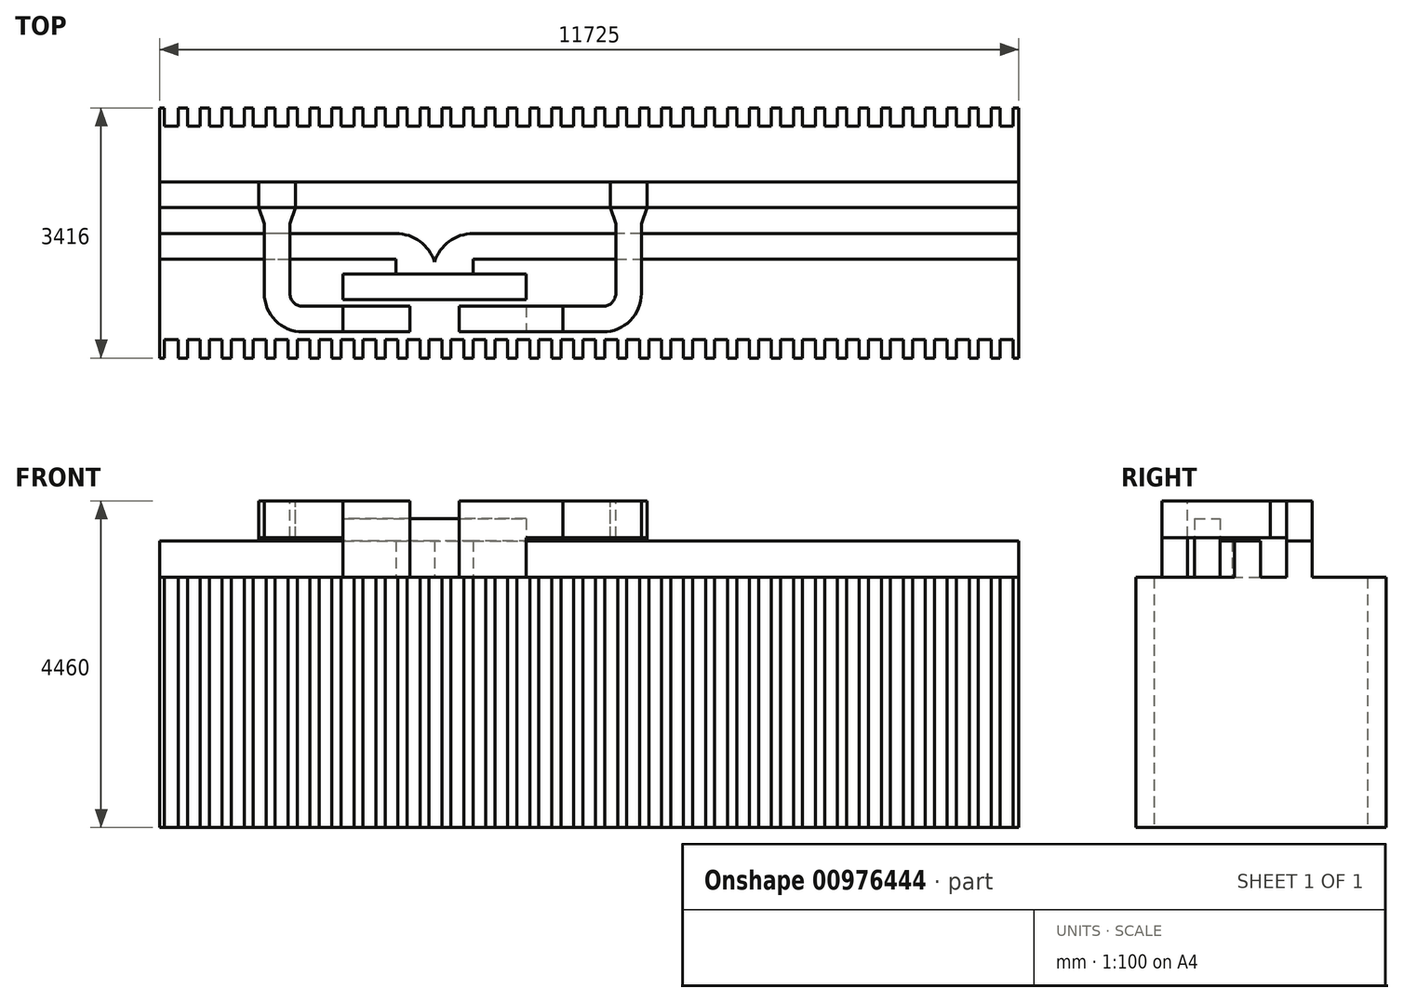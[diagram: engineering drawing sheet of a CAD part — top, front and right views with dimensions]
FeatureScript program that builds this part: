
annotation { "Feature Type Name" : "Feature", "Feature Type Description" : "" }
export const myFeature = defineFeature(function(context is Context, id is Id, definition is map)
    precondition{}
    {
        {
            var Q0;
            Q0=qCreatedBy(makeId("Top.planeOp"),FACE);
            var sketch = newSketch(context, id + "F0", { "sketchPlane" : qUnion([Q0])});
            skLineSegment(sketch, "E0.bottom", {"start": v(-25000, 7300) * mm, "end": v(25000, 7300) * mm});
            skLineSegment(sketch, "E0.top", {"start": v(-25000, -7300) * mm, "end": v(25000, -7300) * mm});
            skLineSegment(sketch, "E0.left", {"start": v(-25000, 7300) * mm, "end": v(-25000, -7300) * mm});
            skLineSegment(sketch, "E0.right", {"start": v(25000, 7300) * mm, "end": v(25000, -7300) * mm});
            skPoint(sketch, "E0.middle", {"position": v(0, 0) * mm});
            skSolve(sketch);
        }
        {
            var Q0;
            Q0=makeQuery(id+"F0.imprint","IMPRINT",FACE,{"disambiguationData":[TD([[makeQuery(id+"F0.imprint","IMPRINT",EDGE,{"derivedFrom":sQuery(id+"F0.wireOp",EDGE,"E0.bottom")}),-1.0]])]});
            var sketch = newSketch(context, id + "F1", { "sketchPlane" : qUnion([Q0])});
            skLineSegment(sketch, "E1", {"start": v(-20201.46, 5909) * mm, "end": v(-20138.96, 5909) * mm});
            skLineSegment(sketch, "E2", {"start": v(-20201.46, 5909) * mm, "end": v(-20201.46, 2493) * mm});
            skLineSegment(sketch, "E3", {"start": v(-20201.46, 2493) * mm, "end": v(-20138.96, 2493) * mm});
            skLineSegment(sketch, "E4", {"start": v(-8476.46, 2493) * mm, "end": v(-8476.46, 5909) * mm});
            skLineSegment(sketch, "E5.0", {"start": v(-20138.96, 5909) * mm, "end": v(-20138.96, 2493) * mm});
            skLineSegment(sketch, "E6.0", {"start": v(-19951.46, 5909) * mm, "end": v(-19951.46, 2493) * mm});
            skLineSegment(sketch, "E7.0", {"start": v(-19651.46, 5909) * mm, "end": v(-19651.46, 2493) * mm});
            skLineSegment(sketch, "E8.0", {"start": v(-19351.46, 5909) * mm, "end": v(-19351.46, 2493) * mm});
            skLineSegment(sketch, "E9.0", {"start": v(-19051.46, 5909) * mm, "end": v(-19051.46, 2493) * mm});
            skLineSegment(sketch, "E10.0", {"start": v(-18751.46, 5909) * mm, "end": v(-18751.46, 2493) * mm});
            skLineSegment(sketch, "E11.0", {"start": v(-18451.46, 5909) * mm, "end": v(-18451.46, 2493) * mm});
            skLineSegment(sketch, "E12.0", {"start": v(-18151.46, 5909) * mm, "end": v(-18151.46, 2493) * mm});
            skLineSegment(sketch, "E13.0", {"start": v(-17851.46, 5909) * mm, "end": v(-17851.46, 2493) * mm});
            skLineSegment(sketch, "E14.0", {"start": v(-17551.46, 5909) * mm, "end": v(-17551.46, 2493) * mm});
            skLineSegment(sketch, "E15.0", {"start": v(-17251.46, 5909) * mm, "end": v(-17251.46, 2493) * mm});
            skLineSegment(sketch, "E16.0", {"start": v(-16951.46, 5909) * mm, "end": v(-16951.46, 2493) * mm});
            skLineSegment(sketch, "E17.0", {"start": v(-16651.46, 5909) * mm, "end": v(-16651.46, 2493) * mm});
            skLineSegment(sketch, "E18.0", {"start": v(-16351.46, 5909) * mm, "end": v(-16351.46, 2493) * mm});
            skLineSegment(sketch, "E19.0", {"start": v(-16051.46, 5909) * mm, "end": v(-16051.46, 2493) * mm});
            skLineSegment(sketch, "E20.0", {"start": v(-15751.46, 5909) * mm, "end": v(-15751.46, 2493) * mm});
            skLineSegment(sketch, "E21.0", {"start": v(-25005, 7305) * mm, "end": v(-25005, -7305) * mm});
            skLineSegment(sketch, "E21.1", {"start": v(25005, 7305) * mm, "end": v(-25005, 7305) * mm});
            skLineSegment(sketch, "E21.2", {"start": v(25005, -7305) * mm, "end": v(25005, 7305) * mm});
            skLineSegment(sketch, "E21.3", {"start": v(-25005, -7305) * mm, "end": v(25005, -7305) * mm});
            skLineSegment(sketch, "E22.0", {"start": v(-15451.46, 5909) * mm, "end": v(-15451.46, 2493) * mm});
            skLineSegment(sketch, "E23.0", {"start": v(-15151.46, 5909) * mm, "end": v(-15151.46, 2493) * mm});
            skLineSegment(sketch, "E24.0", {"start": v(-14851.46, 5909) * mm, "end": v(-14851.46, 2493) * mm});
            skLineSegment(sketch, "E25.0", {"start": v(-14551.46, 5909) * mm, "end": v(-14551.46, 2493) * mm});
            skLineSegment(sketch, "E26.0", {"start": v(-14251.46, 5909) * mm, "end": v(-14251.46, 2493) * mm});
            skLineSegment(sketch, "E27.0", {"start": v(-13951.46, 5909) * mm, "end": v(-13951.46, 2493) * mm});
            skLineSegment(sketch, "E28.0", {"start": v(-13651.46, 5909) * mm, "end": v(-13651.46, 2493) * mm});
            skLineSegment(sketch, "E29.0", {"start": v(-13351.46, 5909) * mm, "end": v(-13351.46, 2493) * mm});
            skLineSegment(sketch, "E30.0", {"start": v(-13051.46, 5909) * mm, "end": v(-13051.46, 2493) * mm});
            skLineSegment(sketch, "E31.0", {"start": v(-12751.46, 5909) * mm, "end": v(-12751.46, 2493) * mm});
            skLineSegment(sketch, "E32.0", {"start": v(-12451.46, 5909) * mm, "end": v(-12451.46, 2493) * mm});
            skLineSegment(sketch, "E33.0", {"start": v(-12151.46, 5909) * mm, "end": v(-12151.46, 2493) * mm});
            skLineSegment(sketch, "E34.0", {"start": v(-11851.46, 5909) * mm, "end": v(-11851.46, 2493) * mm});
            skLineSegment(sketch, "E35.0", {"start": v(-11551.46, 5909) * mm, "end": v(-11551.46, 2493) * mm});
            skLineSegment(sketch, "E36.0", {"start": v(-11251.46, 5909) * mm, "end": v(-11251.46, 2493) * mm});
            skLineSegment(sketch, "E37.0", {"start": v(-10951.46, 5909) * mm, "end": v(-10951.46, 2493) * mm});
            skLineSegment(sketch, "E38.0", {"start": v(-10651.46, 5909) * mm, "end": v(-10651.46, 2493) * mm});
            skLineSegment(sketch, "E39.0", {"start": v(-10351.46, 5909) * mm, "end": v(-10351.46, 2493) * mm});
            skLineSegment(sketch, "E40.0", {"start": v(-10051.46, 5909) * mm, "end": v(-10051.46, 2493) * mm});
            skLineSegment(sketch, "E41.0", {"start": v(-9751.46, 5909) * mm, "end": v(-9751.46, 2493) * mm});
            skLineSegment(sketch, "E42.0", {"start": v(-9451.46, 5909) * mm, "end": v(-9451.46, 2493) * mm});
            skLineSegment(sketch, "E43.0", {"start": v(-9151.46, 5909) * mm, "end": v(-9151.46, 2493) * mm});
            skLineSegment(sketch, "E44.0", {"start": v(-8851.46, 5909) * mm, "end": v(-8851.46, 2493) * mm});
            skLineSegment(sketch, "E45.0", {"start": v(-8551.46, 5909) * mm, "end": v(-8551.46, 2493) * mm});
            skLineSegment(sketch, "E46.0", {"start": v(-19826.46, 5909) * mm, "end": v(-19826.46, 2493) * mm});
            skLineSegment(sketch, "E47.0", {"start": v(-19526.46, 5909) * mm, "end": v(-19526.46, 2493) * mm});
            skLineSegment(sketch, "E48.0", {"start": v(-19226.46, 5909) * mm, "end": v(-19226.46, 2493) * mm});
            skLineSegment(sketch, "E49.0", {"start": v(-18926.46, 5909) * mm, "end": v(-18926.46, 2493) * mm});
            skLineSegment(sketch, "E50.0", {"start": v(-18626.46, 5909) * mm, "end": v(-18626.46, 2493) * mm});
            skLineSegment(sketch, "E51.0", {"start": v(-18326.46, 5909) * mm, "end": v(-18326.46, 2493) * mm});
            skLineSegment(sketch, "E52.0", {"start": v(-18026.46, 5909) * mm, "end": v(-18026.46, 2493) * mm});
            skLineSegment(sketch, "E53.0", {"start": v(-17726.46, 5909) * mm, "end": v(-17726.46, 2493) * mm});
            skLineSegment(sketch, "E54.0", {"start": v(-17426.46, 5909) * mm, "end": v(-17426.46, 2493) * mm});
            skLineSegment(sketch, "E55.0", {"start": v(-17126.46, 5909) * mm, "end": v(-17126.46, 2493) * mm});
            skLineSegment(sketch, "E56.0", {"start": v(-16826.46, 5909) * mm, "end": v(-16826.46, 2493) * mm});
            skLineSegment(sketch, "E57.0", {"start": v(-16526.46, 5909) * mm, "end": v(-16526.46, 2493) * mm});
            skLineSegment(sketch, "E58.0", {"start": v(-16226.46, 5909) * mm, "end": v(-16226.46, 2493) * mm});
            skLineSegment(sketch, "E59.0", {"start": v(-15926.46, 5909) * mm, "end": v(-15926.46, 2493) * mm});
            skLineSegment(sketch, "E60.0", {"start": v(-15626.46, 5909) * mm, "end": v(-15626.46, 2493) * mm});
            skLineSegment(sketch, "E61.0", {"start": v(-15326.46, 5909) * mm, "end": v(-15326.46, 2493) * mm});
            skLineSegment(sketch, "E62.0", {"start": v(-15026.46, 5909) * mm, "end": v(-15026.46, 2493) * mm});
            skLineSegment(sketch, "E63.0", {"start": v(-14726.46, 5909) * mm, "end": v(-14726.46, 2493) * mm});
            skLineSegment(sketch, "E64.0", {"start": v(-14426.46, 5909) * mm, "end": v(-14426.46, 2493) * mm});
            skLineSegment(sketch, "E65.0", {"start": v(-14126.46, 5909) * mm, "end": v(-14126.46, 2493) * mm});
            skLineSegment(sketch, "E66.0", {"start": v(-13826.46, 5909) * mm, "end": v(-13826.46, 2493) * mm});
            skLineSegment(sketch, "E67.0", {"start": v(-13526.46, 5909) * mm, "end": v(-13526.46, 2493) * mm});
            skLineSegment(sketch, "E68.0", {"start": v(-13226.46, 5909) * mm, "end": v(-13226.46, 2493) * mm});
            skLineSegment(sketch, "E69.0", {"start": v(-12926.46, 5909) * mm, "end": v(-12926.46, 2493) * mm});
            skLineSegment(sketch, "E70.0", {"start": v(-12626.46, 5909) * mm, "end": v(-12626.46, 2493) * mm});
            skLineSegment(sketch, "E71.0", {"start": v(-12326.46, 5909) * mm, "end": v(-12326.46, 2493) * mm});
            skLineSegment(sketch, "E72.0", {"start": v(-12026.46, 5909) * mm, "end": v(-12026.46, 2493) * mm});
            skLineSegment(sketch, "E73.0", {"start": v(-11726.46, 5909) * mm, "end": v(-11726.46, 2493) * mm});
            skLineSegment(sketch, "E74.0", {"start": v(-11426.46, 5909) * mm, "end": v(-11426.46, 2493) * mm});
            skLineSegment(sketch, "E75.0", {"start": v(-11126.46, 5909) * mm, "end": v(-11126.46, 2493) * mm});
            skLineSegment(sketch, "E76.0", {"start": v(-10826.46, 5909) * mm, "end": v(-10826.46, 2493) * mm});
            skLineSegment(sketch, "E77.0", {"start": v(-10526.46, 5909) * mm, "end": v(-10526.46, 2493) * mm});
            skLineSegment(sketch, "E78.0", {"start": v(-10226.46, 5909) * mm, "end": v(-10226.46, 2493) * mm});
            skLineSegment(sketch, "E79.0", {"start": v(-9926.46, 5909) * mm, "end": v(-9926.46, 2493) * mm});
            skLineSegment(sketch, "E80.0", {"start": v(-9626.46, 5909) * mm, "end": v(-9626.46, 2493) * mm});
            skLineSegment(sketch, "E81.0", {"start": v(-9326.46, 5909) * mm, "end": v(-9326.46, 2493) * mm});
            skLineSegment(sketch, "E82.0", {"start": v(-9026.46, 5909) * mm, "end": v(-9026.46, 2493) * mm});
            skLineSegment(sketch, "E83.0", {"start": v(-8726.46, 5909) * mm, "end": v(-8726.46, 2493) * mm});
            skLineSegment(sketch, "E84", {"start": v(-20201.46, 5659) * mm, "end": v(-8476.46, 5659) * mm});
            skLineSegment(sketch, "E85", {"start": v(-20201.46, 2743) * mm, "end": v(-8476.46, 2743) * mm});
            skLineSegment(sketch, "E86.trimOffspring", {"start": v(-8551.46, 5909) * mm, "end": v(-8476.46, 5909) * mm});
            skLineSegment(sketch, "E87.trimOffspring", {"start": v(-8851.46, 5909) * mm, "end": v(-8726.46, 5909) * mm});
            skLineSegment(sketch, "E88.trimOffspring", {"start": v(-9151.46, 5909) * mm, "end": v(-9026.46, 5909) * mm});
            skLineSegment(sketch, "E89.trimOffspring", {"start": v(-9451.46, 5909) * mm, "end": v(-9326.46, 5909) * mm});
            skLineSegment(sketch, "E90.trimOffspring", {"start": v(-9751.46, 5909) * mm, "end": v(-9626.46, 5909) * mm});
            skLineSegment(sketch, "E91.trimOffspring", {"start": v(-10051.46, 5909) * mm, "end": v(-9926.46, 5909) * mm});
            skLineSegment(sketch, "E92.trimOffspring", {"start": v(-10351.46, 5909) * mm, "end": v(-10226.46, 5909) * mm});
            skLineSegment(sketch, "E93.trimOffspring", {"start": v(-10651.46, 5909) * mm, "end": v(-10526.46, 5909) * mm});
            skLineSegment(sketch, "E94.trimOffspring", {"start": v(-10951.46, 5909) * mm, "end": v(-10826.46, 5909) * mm});
            skLineSegment(sketch, "E95.trimOffspring", {"start": v(-11251.46, 5909) * mm, "end": v(-11126.46, 5909) * mm});
            skLineSegment(sketch, "E96.trimOffspring", {"start": v(-11551.46, 5909) * mm, "end": v(-11426.46, 5909) * mm});
            skLineSegment(sketch, "E97.trimOffspring", {"start": v(-11851.46, 5909) * mm, "end": v(-11726.46, 5909) * mm});
            skLineSegment(sketch, "E98.trimOffspring", {"start": v(-12151.46, 5909) * mm, "end": v(-12026.46, 5909) * mm});
            skLineSegment(sketch, "E99.trimOffspring", {"start": v(-12451.46, 5909) * mm, "end": v(-12326.46, 5909) * mm});
            skLineSegment(sketch, "E100.trimOffspring", {"start": v(-12751.46, 5909) * mm, "end": v(-12626.46, 5909) * mm});
            skLineSegment(sketch, "E101.trimOffspring", {"start": v(-13051.46, 5909) * mm, "end": v(-12926.46, 5909) * mm});
            skLineSegment(sketch, "E102.trimOffspring", {"start": v(-13351.46, 5909) * mm, "end": v(-13226.46, 5909) * mm});
            skLineSegment(sketch, "E103.trimOffspring", {"start": v(-13651.46, 5909) * mm, "end": v(-13526.46, 5909) * mm});
            skLineSegment(sketch, "E104.trimOffspring", {"start": v(-13951.46, 5909) * mm, "end": v(-13826.46, 5909) * mm});
            skLineSegment(sketch, "E105.trimOffspring", {"start": v(-14251.46, 5909) * mm, "end": v(-14126.46, 5909) * mm});
            skLineSegment(sketch, "E106.trimOffspring", {"start": v(-14551.46, 5909) * mm, "end": v(-14426.46, 5909) * mm});
            skLineSegment(sketch, "E107.trimOffspring", {"start": v(-14851.46, 5909) * mm, "end": v(-14726.46, 5909) * mm});
            skLineSegment(sketch, "E108.trimOffspring", {"start": v(-15151.46, 5909) * mm, "end": v(-15026.46, 5909) * mm});
            skLineSegment(sketch, "E109.trimOffspring", {"start": v(-15451.46, 5909) * mm, "end": v(-15326.46, 5909) * mm});
            skLineSegment(sketch, "E110.trimOffspring", {"start": v(-15751.46, 5909) * mm, "end": v(-15626.46, 5909) * mm});
            skLineSegment(sketch, "E111.trimOffspring", {"start": v(-16051.46, 5909) * mm, "end": v(-15926.46, 5909) * mm});
            skLineSegment(sketch, "E112.trimOffspring", {"start": v(-16351.46, 5909) * mm, "end": v(-16226.46, 5909) * mm});
            skLineSegment(sketch, "E113.trimOffspring", {"start": v(-16651.46, 5909) * mm, "end": v(-16526.46, 5909) * mm});
            skLineSegment(sketch, "E114.trimOffspring", {"start": v(-16951.46, 5909) * mm, "end": v(-16826.46, 5909) * mm});
            skLineSegment(sketch, "E115.trimOffspring", {"start": v(-17251.46, 5909) * mm, "end": v(-17126.46, 5909) * mm});
            skLineSegment(sketch, "E116.trimOffspring", {"start": v(-17551.46, 5909) * mm, "end": v(-17426.46, 5909) * mm});
            skLineSegment(sketch, "E117.trimOffspring", {"start": v(-17851.46, 5909) * mm, "end": v(-17726.46, 5909) * mm});
            skLineSegment(sketch, "E118.trimOffspring", {"start": v(-18151.46, 5909) * mm, "end": v(-18026.46, 5909) * mm});
            skLineSegment(sketch, "E119.trimOffspring", {"start": v(-18451.46, 5909) * mm, "end": v(-18326.46, 5909) * mm});
            skLineSegment(sketch, "E120.trimOffspring", {"start": v(-18751.46, 5909) * mm, "end": v(-18626.46, 5909) * mm});
            skLineSegment(sketch, "E121.trimOffspring", {"start": v(-19051.46, 5909) * mm, "end": v(-18926.46, 5909) * mm});
            skLineSegment(sketch, "E122.trimOffspring", {"start": v(-19351.46, 5909) * mm, "end": v(-19226.46, 5909) * mm});
            skLineSegment(sketch, "E123.trimOffspring", {"start": v(-19651.46, 5909) * mm, "end": v(-19526.46, 5909) * mm});
            skLineSegment(sketch, "E124.trimOffspring", {"start": v(-19951.46, 5909) * mm, "end": v(-19826.46, 5909) * mm});
            skLineSegment(sketch, "E125.trimOffspring", {"start": v(-19651.46, 2493) * mm, "end": v(-19526.46, 2493) * mm});
            skLineSegment(sketch, "E126.trimOffspring", {"start": v(-18751.46, 2493) * mm, "end": v(-18626.46, 2493) * mm});
            skLineSegment(sketch, "E127.trimOffspring", {"start": v(-17851.46, 2493) * mm, "end": v(-17726.46, 2493) * mm});
            skLineSegment(sketch, "E128.trimOffspring", {"start": v(-17251.46, 2493) * mm, "end": v(-17126.46, 2493) * mm});
            skLineSegment(sketch, "E129.trimOffspring", {"start": v(-16351.46, 2493) * mm, "end": v(-16226.46, 2493) * mm});
            skLineSegment(sketch, "E130.trimOffspring", {"start": v(-16951.46, 2493) * mm, "end": v(-16826.46, 2493) * mm});
            skLineSegment(sketch, "E131", {"start": v(-17551.46, 2493) * mm, "end": v(-17426.46, 2493) * mm});
            skLineSegment(sketch, "E132", {"start": v(-16651.46, 2493) * mm, "end": v(-16526.46, 2493) * mm});
            skLineSegment(sketch, "E133.trimOffspring", {"start": v(-15751.46, 2493) * mm, "end": v(-15626.46, 2493) * mm});
            skLineSegment(sketch, "E134.trimOffspring", {"start": v(-14551.46, 2493) * mm, "end": v(-14426.46, 2493) * mm});
            skLineSegment(sketch, "E135.trimOffspring", {"start": v(-15151.46, 2493) * mm, "end": v(-15026.46, 2493) * mm});
            skLineSegment(sketch, "E136.trimOffspring", {"start": v(-15451.46, 2493) * mm, "end": v(-15326.46, 2493) * mm});
            skLineSegment(sketch, "E137", {"start": v(-14851.46, 2493) * mm, "end": v(-14726.46, 2493) * mm});
            skLineSegment(sketch, "E138.trimOffspring", {"start": v(-13951.46, 2493) * mm, "end": v(-13826.46, 2493) * mm});
            skLineSegment(sketch, "E139.trimOffspring", {"start": v(-13351.46, 2493) * mm, "end": v(-13226.46, 2493) * mm});
            skLineSegment(sketch, "E140.trimOffspring", {"start": v(-13651.46, 2493) * mm, "end": v(-13526.46, 2493) * mm});
            skLineSegment(sketch, "E141", {"start": v(-14251.46, 2493) * mm, "end": v(-14126.46, 2493) * mm});
            skLineSegment(sketch, "E142.trimOffspring", {"start": v(-13051.46, 2493) * mm, "end": v(-12926.46, 2493) * mm});
            skLineSegment(sketch, "E143.trimOffspring", {"start": v(-12751.46, 2493) * mm, "end": v(-12626.46, 2493) * mm});
            skLineSegment(sketch, "E144.trimOffspring", {"start": v(-12151.46, 2493) * mm, "end": v(-12026.46, 2493) * mm});
            skLineSegment(sketch, "E145.trimOffspring", {"start": v(-11551.46, 2493) * mm, "end": v(-11426.46, 2493) * mm});
            skLineSegment(sketch, "E146.trimOffspring", {"start": v(-11851.46, 2493) * mm, "end": v(-11726.46, 2493) * mm});
            skLineSegment(sketch, "E147.trimOffspring", {"start": v(-11251.46, 2493) * mm, "end": v(-11126.46, 2493) * mm});
            skLineSegment(sketch, "E148.trimOffspring", {"start": v(-10951.46, 2493) * mm, "end": v(-10826.46, 2493) * mm});
            skLineSegment(sketch, "E149.trimOffspring", {"start": v(-10651.46, 2493) * mm, "end": v(-10526.46, 2493) * mm});
            skLineSegment(sketch, "E150.trimOffspring", {"start": v(-9751.46, 2493) * mm, "end": v(-9626.46, 2493) * mm});
            skLineSegment(sketch, "E151.trimOffspring", {"start": v(-8851.46, 2493) * mm, "end": v(-8726.46, 2493) * mm});
            skLineSegment(sketch, "E152", {"start": v(-10351.46, 2493) * mm, "end": v(-10226.46, 2493) * mm});
            skLineSegment(sketch, "E153", {"start": v(-10051.46, 2493) * mm, "end": v(-9926.46, 2493) * mm});
            skLineSegment(sketch, "E154", {"start": v(-9151.46, 2493) * mm, "end": v(-9026.46, 2493) * mm});
            skLineSegment(sketch, "E155.trimOffspring", {"start": v(-9451.46, 2493) * mm, "end": v(-9326.46, 2493) * mm});
            skLineSegment(sketch, "E156.trimOffspring", {"start": v(-8551.46, 2493) * mm, "end": v(-8476.46, 2493) * mm});
            skLineSegment(sketch, "E157.trimOffspring", {"start": v(-18451.46, 2493) * mm, "end": v(-18326.46, 2493) * mm});
            skLineSegment(sketch, "E158.trimOffspring", {"start": v(-19351.46, 2493) * mm, "end": v(-19226.46, 2493) * mm});
            skLineSegment(sketch, "E159", {"start": v(-19051.46, 2493) * mm, "end": v(-18926.46, 2493) * mm});
            skLineSegment(sketch, "E160", {"start": v(-18151.46, 2493) * mm, "end": v(-18026.46, 2493) * mm});
            skLineSegment(sketch, "E161", {"start": v(-16051.46, 2493) * mm, "end": v(-15926.46, 2493) * mm});
            skLineSegment(sketch, "E162", {"start": v(-19951.46, 2493) * mm, "end": v(-19826.46, 2493) * mm});
            skLineSegment(sketch, "E163", {"start": v(-12451.46, 2493) * mm, "end": v(-12326.46, 2493) * mm});
            skSolve(sketch);
        }
        {
            var Q0;
            {var subQ0=sQuery(id+"F1.wireOp",EDGE,"E88.trimOffspring");Q0=makeQuery(id+"F1.imprint","IMPRINT",FACE,{"disambiguationData":[TD([[makeQuery(id+"F1.imprint","IMPRINT",EDGE,{"derivedFrom":subQ0}),-1.0]])]});}
            var Q1;
            {var subQ0=sQuery(id+"F1.wireOp",EDGE,"E112.trimOffspring");Q1=makeQuery(id+"F1.imprint","IMPRINT",FACE,{"disambiguationData":[TD([[makeQuery(id+"F1.imprint","IMPRINT",EDGE,{"derivedFrom":subQ0}),-1.0]])]});}
            var Q2;
            {var subQ0=sQuery(id+"F1.wireOp",EDGE,"E84");var subQ1=sQuery(id+"F1.wireOp",EDGE,"E38.0");var subQ2=makeQuery(id+"F1.imprint","INTERSECT",VERTEX,{"derivedFrom":[subQ1,subQ0]});Q2=makeQuery(id+"F1.imprint","IMPRINT",FACE,{"disambiguationData":[TD([[makeQuery(id+"F1.imprint","IMPRINT",EDGE,{"disambiguationData":[TD([[subQ2,-1.0]])],"derivedFrom":subQ1}),1.0]])]});}
            var Q3;
            {var subQ0=sQuery(id+"F1.wireOp",EDGE,"E158.trimOffspring");Q3=makeQuery(id+"F1.imprint","IMPRINT",FACE,{"disambiguationData":[TD([[makeQuery(id+"F1.imprint","IMPRINT",EDGE,{"derivedFrom":subQ0}),1.0]])]});}
            var Q4;
            {var subQ0=sQuery(id+"F1.wireOp",EDGE,"E84");var subQ1=sQuery(id+"F1.wireOp",EDGE,"E18.0");var subQ2=makeQuery(id+"F1.imprint","INTERSECT",VERTEX,{"derivedFrom":[subQ1,subQ0]});Q4=makeQuery(id+"F1.imprint","IMPRINT",FACE,{"disambiguationData":[TD([[makeQuery(id+"F1.imprint","IMPRINT",EDGE,{"disambiguationData":[TD([[subQ2,-1.0]])],"derivedFrom":subQ1}),-1.0]])]});}
            var Q5;
            {var subQ0=sQuery(id+"F1.wireOp",EDGE,"E140.trimOffspring");Q5=makeQuery(id+"F1.imprint","IMPRINT",FACE,{"disambiguationData":[TD([[makeQuery(id+"F1.imprint","IMPRINT",EDGE,{"derivedFrom":subQ0}),1.0]])]});}
            var Q6;
            {var subQ0=sQuery(id+"F1.wireOp",EDGE,"E84");var subQ1=sQuery(id+"F1.wireOp",EDGE,"E35.0");var subQ2=makeQuery(id+"F1.imprint","INTERSECT",VERTEX,{"derivedFrom":[subQ1,subQ0]});Q6=makeQuery(id+"F1.imprint","IMPRINT",FACE,{"disambiguationData":[TD([[makeQuery(id+"F1.imprint","IMPRINT",EDGE,{"disambiguationData":[TD([[subQ2,-1.0]])],"derivedFrom":subQ1}),-1.0]])]});}
            var Q7;
            {var subQ0=sQuery(id+"F1.wireOp",EDGE,"E107.trimOffspring");Q7=makeQuery(id+"F1.imprint","IMPRINT",FACE,{"disambiguationData":[TD([[makeQuery(id+"F1.imprint","IMPRINT",EDGE,{"derivedFrom":subQ0}),-1.0]])]});}
            var Q8;
            {var subQ0=sQuery(id+"F1.wireOp",EDGE,"E129.trimOffspring");Q8=makeQuery(id+"F1.imprint","IMPRINT",FACE,{"disambiguationData":[TD([[makeQuery(id+"F1.imprint","IMPRINT",EDGE,{"derivedFrom":subQ0}),1.0]])]});}
            var Q9;
            {var subQ0=sQuery(id+"F1.wireOp",EDGE,"E120.trimOffspring");Q9=makeQuery(id+"F1.imprint","IMPRINT",FACE,{"disambiguationData":[TD([[makeQuery(id+"F1.imprint","IMPRINT",EDGE,{"derivedFrom":subQ0}),-1.0]])]});}
            var Q10;
            {var subQ0=sQuery(id+"F1.wireOp",EDGE,"E115.trimOffspring");Q10=makeQuery(id+"F1.imprint","IMPRINT",FACE,{"disambiguationData":[TD([[makeQuery(id+"F1.imprint","IMPRINT",EDGE,{"derivedFrom":subQ0}),-1.0]])]});}
            var Q11;
            {var subQ0=sQuery(id+"F1.wireOp",EDGE,"E138.trimOffspring");Q11=makeQuery(id+"F1.imprint","IMPRINT",FACE,{"disambiguationData":[TD([[makeQuery(id+"F1.imprint","IMPRINT",EDGE,{"derivedFrom":subQ0}),1.0]])]});}
            var Q12;
            {var subQ0=sQuery(id+"F1.wireOp",EDGE,"E84");var subQ1=sQuery(id+"F1.wireOp",EDGE,"E11.0");var subQ2=makeQuery(id+"F1.imprint","INTERSECT",VERTEX,{"derivedFrom":[subQ1,subQ0]});Q12=makeQuery(id+"F1.imprint","IMPRINT",FACE,{"disambiguationData":[TD([[makeQuery(id+"F1.imprint","IMPRINT",EDGE,{"disambiguationData":[TD([[subQ2,-1.0]])],"derivedFrom":subQ1}),1.0]])]});}
            var Q13;
            {var subQ0=sQuery(id+"F1.wireOp",EDGE,"E91.trimOffspring");Q13=makeQuery(id+"F1.imprint","IMPRINT",FACE,{"disambiguationData":[TD([[makeQuery(id+"F1.imprint","IMPRINT",EDGE,{"derivedFrom":subQ0}),-1.0]])]});}
            var Q14;
            {var subQ0=sQuery(id+"F1.wireOp",EDGE,"E84");var subQ1=sQuery(id+"F1.wireOp",EDGE,"E13.0");var subQ2=makeQuery(id+"F1.imprint","INTERSECT",VERTEX,{"derivedFrom":[subQ1,subQ0]});Q14=makeQuery(id+"F1.imprint","IMPRINT",FACE,{"disambiguationData":[TD([[makeQuery(id+"F1.imprint","IMPRINT",EDGE,{"disambiguationData":[TD([[subQ2,-1.0]])],"derivedFrom":subQ1}),-1.0]])]});}
            var Q15;
            {var subQ0=sQuery(id+"F1.wireOp",EDGE,"E84");var subQ1=sQuery(id+"F1.wireOp",EDGE,"E26.0");var subQ2=makeQuery(id+"F1.imprint","INTERSECT",VERTEX,{"derivedFrom":[subQ1,subQ0]});Q15=makeQuery(id+"F1.imprint","IMPRINT",FACE,{"disambiguationData":[TD([[makeQuery(id+"F1.imprint","IMPRINT",EDGE,{"disambiguationData":[TD([[subQ2,-1.0]])],"derivedFrom":subQ1}),-1.0]])]});}
            var Q16;
            {var subQ0=sQuery(id+"F1.wireOp",EDGE,"E121.trimOffspring");Q16=makeQuery(id+"F1.imprint","IMPRINT",FACE,{"disambiguationData":[TD([[makeQuery(id+"F1.imprint","IMPRINT",EDGE,{"derivedFrom":subQ0}),-1.0]])]});}
            var Q17;
            {var subQ0=sQuery(id+"F1.wireOp",EDGE,"E130.trimOffspring");Q17=makeQuery(id+"F1.imprint","IMPRINT",FACE,{"disambiguationData":[TD([[makeQuery(id+"F1.imprint","IMPRINT",EDGE,{"derivedFrom":subQ0}),1.0]])]});}
            var Q18;
            {var subQ0=sQuery(id+"F1.wireOp",EDGE,"E154");Q18=makeQuery(id+"F1.imprint","IMPRINT",FACE,{"disambiguationData":[TD([[makeQuery(id+"F1.imprint","IMPRINT",EDGE,{"derivedFrom":subQ0}),1.0]])]});}
            var Q19;
            {var subQ0=sQuery(id+"F1.wireOp",EDGE,"E151.trimOffspring");Q19=makeQuery(id+"F1.imprint","IMPRINT",FACE,{"disambiguationData":[TD([[makeQuery(id+"F1.imprint","IMPRINT",EDGE,{"derivedFrom":subQ0}),1.0]])]});}
            var Q20;
            {var subQ0=sQuery(id+"F1.wireOp",EDGE,"E84");var subQ1=sQuery(id+"F1.wireOp",EDGE,"E30.0");var subQ2=makeQuery(id+"F1.imprint","INTERSECT",VERTEX,{"derivedFrom":[subQ1,subQ0]});Q20=makeQuery(id+"F1.imprint","IMPRINT",FACE,{"disambiguationData":[TD([[makeQuery(id+"F1.imprint","IMPRINT",EDGE,{"disambiguationData":[TD([[subQ2,-1.0]])],"derivedFrom":subQ1}),-1.0]])]});}
            var Q21;
            {var subQ0=sQuery(id+"F1.wireOp",EDGE,"E84");var subQ1=sQuery(id+"F1.wireOp",EDGE,"E19.0");var subQ2=makeQuery(id+"F1.imprint","INTERSECT",VERTEX,{"derivedFrom":[subQ1,subQ0]});Q21=makeQuery(id+"F1.imprint","IMPRINT",FACE,{"disambiguationData":[TD([[makeQuery(id+"F1.imprint","IMPRINT",EDGE,{"disambiguationData":[TD([[subQ2,-1.0]])],"derivedFrom":subQ1}),1.0]])]});}
            var Q22;
            {var subQ0=sQuery(id+"F1.wireOp",EDGE,"E84");var subQ1=sQuery(id+"F1.wireOp",EDGE,"E14.0");var subQ2=makeQuery(id+"F1.imprint","INTERSECT",VERTEX,{"derivedFrom":[subQ1,subQ0]});Q22=makeQuery(id+"F1.imprint","IMPRINT",FACE,{"disambiguationData":[TD([[makeQuery(id+"F1.imprint","IMPRINT",EDGE,{"disambiguationData":[TD([[subQ2,-1.0]])],"derivedFrom":subQ1}),-1.0]])]});}
            var Q23;
            {var subQ0=sQuery(id+"F1.wireOp",EDGE,"E84");var subQ1=sQuery(id+"F1.wireOp",EDGE,"E12.0");var subQ2=makeQuery(id+"F1.imprint","INTERSECT",VERTEX,{"derivedFrom":[subQ1,subQ0]});Q23=makeQuery(id+"F1.imprint","IMPRINT",FACE,{"disambiguationData":[TD([[makeQuery(id+"F1.imprint","IMPRINT",EDGE,{"disambiguationData":[TD([[subQ2,-1.0]])],"derivedFrom":subQ1}),1.0]])]});}
            var Q24;
            {var subQ0=sQuery(id+"F1.wireOp",EDGE,"E143.trimOffspring");Q24=makeQuery(id+"F1.imprint","IMPRINT",FACE,{"disambiguationData":[TD([[makeQuery(id+"F1.imprint","IMPRINT",EDGE,{"derivedFrom":subQ0}),1.0]])]});}
            var Q25;
            {var subQ0=sQuery(id+"F1.wireOp",EDGE,"E161");Q25=makeQuery(id+"F1.imprint","IMPRINT",FACE,{"disambiguationData":[TD([[makeQuery(id+"F1.imprint","IMPRINT",EDGE,{"derivedFrom":subQ0}),1.0]])]});}
            var Q26;
            {var subQ0=sQuery(id+"F1.wireOp",EDGE,"E100.trimOffspring");Q26=makeQuery(id+"F1.imprint","IMPRINT",FACE,{"disambiguationData":[TD([[makeQuery(id+"F1.imprint","IMPRINT",EDGE,{"derivedFrom":subQ0}),-1.0]])]});}
            var Q27;
            {var subQ0=sQuery(id+"F1.wireOp",EDGE,"E84");var subQ1=sQuery(id+"F1.wireOp",EDGE,"E15.0");var subQ2=makeQuery(id+"F1.imprint","INTERSECT",VERTEX,{"derivedFrom":[subQ1,subQ0]});Q27=makeQuery(id+"F1.imprint","IMPRINT",FACE,{"disambiguationData":[TD([[makeQuery(id+"F1.imprint","IMPRINT",EDGE,{"disambiguationData":[TD([[subQ2,-1.0]])],"derivedFrom":subQ1}),-1.0]])]});}
            var Q28;
            {var subQ0=sQuery(id+"F1.wireOp",EDGE,"E84");var subQ1=sQuery(id+"F1.wireOp",EDGE,"E39.0");var subQ2=makeQuery(id+"F1.imprint","INTERSECT",VERTEX,{"derivedFrom":[subQ1,subQ0]});Q28=makeQuery(id+"F1.imprint","IMPRINT",FACE,{"disambiguationData":[TD([[makeQuery(id+"F1.imprint","IMPRINT",EDGE,{"disambiguationData":[TD([[subQ2,-1.0]])],"derivedFrom":subQ1}),1.0]])]});}
            var Q29;
            {var subQ0=sQuery(id+"F1.wireOp",EDGE,"E84");var subQ1=sQuery(id+"F1.wireOp",EDGE,"E36.0");var subQ2=makeQuery(id+"F1.imprint","INTERSECT",VERTEX,{"derivedFrom":[subQ1,subQ0]});Q29=makeQuery(id+"F1.imprint","IMPRINT",FACE,{"disambiguationData":[TD([[makeQuery(id+"F1.imprint","IMPRINT",EDGE,{"disambiguationData":[TD([[subQ2,-1.0]])],"derivedFrom":subQ1}),1.0]])]});}
            var Q30;
            {var subQ0=sQuery(id+"F1.wireOp",EDGE,"E84");var subQ1=sQuery(id+"F1.wireOp",EDGE,"E40.0");var subQ2=makeQuery(id+"F1.imprint","INTERSECT",VERTEX,{"derivedFrom":[subQ1,subQ0]});Q30=makeQuery(id+"F1.imprint","IMPRINT",FACE,{"disambiguationData":[TD([[makeQuery(id+"F1.imprint","IMPRINT",EDGE,{"disambiguationData":[TD([[subQ2,-1.0]])],"derivedFrom":subQ1}),1.0]])]});}
            var Q31;
            {var subQ0=sQuery(id+"F1.wireOp",EDGE,"E118.trimOffspring");Q31=makeQuery(id+"F1.imprint","IMPRINT",FACE,{"disambiguationData":[TD([[makeQuery(id+"F1.imprint","IMPRINT",EDGE,{"derivedFrom":subQ0}),-1.0]])]});}
            var Q32;
            {var subQ0=sQuery(id+"F1.wireOp",EDGE,"E84");var subQ1=sQuery(id+"F1.wireOp",EDGE,"E10.0");var subQ2=makeQuery(id+"F1.imprint","INTERSECT",VERTEX,{"derivedFrom":[subQ1,subQ0]});Q32=makeQuery(id+"F1.imprint","IMPRINT",FACE,{"disambiguationData":[TD([[makeQuery(id+"F1.imprint","IMPRINT",EDGE,{"disambiguationData":[TD([[subQ2,-1.0]])],"derivedFrom":subQ1}),-1.0]])]});}
            var Q33;
            {var subQ0=sQuery(id+"F1.wireOp",EDGE,"E84");var subQ1=sQuery(id+"F1.wireOp",EDGE,"E19.0");var subQ2=makeQuery(id+"F1.imprint","INTERSECT",VERTEX,{"derivedFrom":[subQ1,subQ0]});Q33=makeQuery(id+"F1.imprint","IMPRINT",FACE,{"disambiguationData":[TD([[makeQuery(id+"F1.imprint","IMPRINT",EDGE,{"disambiguationData":[TD([[subQ2,-1.0]])],"derivedFrom":subQ1}),-1.0]])]});}
            var Q34;
            {var subQ0=sQuery(id+"F1.wireOp",EDGE,"E84");var subQ1=sQuery(id+"F1.wireOp",EDGE,"E29.0");var subQ2=makeQuery(id+"F1.imprint","INTERSECT",VERTEX,{"derivedFrom":[subQ1,subQ0]});Q34=makeQuery(id+"F1.imprint","IMPRINT",FACE,{"disambiguationData":[TD([[makeQuery(id+"F1.imprint","IMPRINT",EDGE,{"disambiguationData":[TD([[subQ2,-1.0]])],"derivedFrom":subQ1}),-1.0]])]});}
            var Q35;
            {var subQ0=sQuery(id+"F1.wireOp",EDGE,"E84");var subQ1=sQuery(id+"F1.wireOp",EDGE,"E9.0");var subQ2=makeQuery(id+"F1.imprint","INTERSECT",VERTEX,{"derivedFrom":[subQ1,subQ0]});Q35=makeQuery(id+"F1.imprint","IMPRINT",FACE,{"disambiguationData":[TD([[makeQuery(id+"F1.imprint","IMPRINT",EDGE,{"disambiguationData":[TD([[subQ2,-1.0]])],"derivedFrom":subQ1}),-1.0]])]});}
            var Q36;
            {var subQ0=sQuery(id+"F1.wireOp",EDGE,"E102.trimOffspring");Q36=makeQuery(id+"F1.imprint","IMPRINT",FACE,{"disambiguationData":[TD([[makeQuery(id+"F1.imprint","IMPRINT",EDGE,{"derivedFrom":subQ0}),-1.0]])]});}
            var Q37;
            {var subQ0=sQuery(id+"F1.wireOp",EDGE,"E99.trimOffspring");Q37=makeQuery(id+"F1.imprint","IMPRINT",FACE,{"disambiguationData":[TD([[makeQuery(id+"F1.imprint","IMPRINT",EDGE,{"derivedFrom":subQ0}),-1.0]])]});}
            var Q38;
            {var subQ0=sQuery(id+"F1.wireOp",EDGE,"E117.trimOffspring");Q38=makeQuery(id+"F1.imprint","IMPRINT",FACE,{"disambiguationData":[TD([[makeQuery(id+"F1.imprint","IMPRINT",EDGE,{"derivedFrom":subQ0}),-1.0]])]});}
            var Q39;
            {var subQ0=sQuery(id+"F1.wireOp",EDGE,"E84");var subQ1=sQuery(id+"F1.wireOp",EDGE,"E17.0");var subQ2=makeQuery(id+"F1.imprint","INTERSECT",VERTEX,{"derivedFrom":[subQ1,subQ0]});Q39=makeQuery(id+"F1.imprint","IMPRINT",FACE,{"disambiguationData":[TD([[makeQuery(id+"F1.imprint","IMPRINT",EDGE,{"disambiguationData":[TD([[subQ2,-1.0]])],"derivedFrom":subQ1}),-1.0]])]});}
            var Q40;
            {var subQ0=sQuery(id+"F1.wireOp",EDGE,"E84");var subQ1=sQuery(id+"F1.wireOp",EDGE,"E33.0");var subQ2=makeQuery(id+"F1.imprint","INTERSECT",VERTEX,{"derivedFrom":[subQ1,subQ0]});Q40=makeQuery(id+"F1.imprint","IMPRINT",FACE,{"disambiguationData":[TD([[makeQuery(id+"F1.imprint","IMPRINT",EDGE,{"disambiguationData":[TD([[subQ2,-1.0]])],"derivedFrom":subQ1}),-1.0]])]});}
            var Q41;
            {var subQ0=sQuery(id+"F1.wireOp",EDGE,"E146.trimOffspring");Q41=makeQuery(id+"F1.imprint","IMPRINT",FACE,{"disambiguationData":[TD([[makeQuery(id+"F1.imprint","IMPRINT",EDGE,{"derivedFrom":subQ0}),1.0]])]});}
            var Q42;
            {var subQ0=sQuery(id+"F1.wireOp",EDGE,"E95.trimOffspring");Q42=makeQuery(id+"F1.imprint","IMPRINT",FACE,{"disambiguationData":[TD([[makeQuery(id+"F1.imprint","IMPRINT",EDGE,{"derivedFrom":subQ0}),-1.0]])]});}
            var Q43;
            {var subQ0=sQuery(id+"F1.wireOp",EDGE,"E134.trimOffspring");Q43=makeQuery(id+"F1.imprint","IMPRINT",FACE,{"disambiguationData":[TD([[makeQuery(id+"F1.imprint","IMPRINT",EDGE,{"derivedFrom":subQ0}),1.0]])]});}
            var Q44;
            {var subQ0=sQuery(id+"F1.wireOp",EDGE,"E122.trimOffspring");Q44=makeQuery(id+"F1.imprint","IMPRINT",FACE,{"disambiguationData":[TD([[makeQuery(id+"F1.imprint","IMPRINT",EDGE,{"derivedFrom":subQ0}),-1.0]])]});}
            var Q45;
            {var subQ0=sQuery(id+"F1.wireOp",EDGE,"E105.trimOffspring");Q45=makeQuery(id+"F1.imprint","IMPRINT",FACE,{"disambiguationData":[TD([[makeQuery(id+"F1.imprint","IMPRINT",EDGE,{"derivedFrom":subQ0}),-1.0]])]});}
            var Q46;
            {var subQ0=sQuery(id+"F1.wireOp",EDGE,"E84");var subQ1=sQuery(id+"F1.wireOp",EDGE,"E31.0");var subQ2=makeQuery(id+"F1.imprint","INTERSECT",VERTEX,{"derivedFrom":[subQ1,subQ0]});Q46=makeQuery(id+"F1.imprint","IMPRINT",FACE,{"disambiguationData":[TD([[makeQuery(id+"F1.imprint","IMPRINT",EDGE,{"disambiguationData":[TD([[subQ2,-1.0]])],"derivedFrom":subQ1}),-1.0]])]});}
            var Q47;
            {var subQ0=sQuery(id+"F1.wireOp",EDGE,"E84");var subQ1=sQuery(id+"F1.wireOp",EDGE,"E24.0");var subQ2=makeQuery(id+"F1.imprint","INTERSECT",VERTEX,{"derivedFrom":[subQ1,subQ0]});Q47=makeQuery(id+"F1.imprint","IMPRINT",FACE,{"disambiguationData":[TD([[makeQuery(id+"F1.imprint","IMPRINT",EDGE,{"disambiguationData":[TD([[subQ2,-1.0]])],"derivedFrom":subQ1}),1.0]])]});}
            var Q48;
            {var subQ0=sQuery(id+"F1.wireOp",EDGE,"E84");var subQ1=sQuery(id+"F1.wireOp",EDGE,"E43.0");var subQ2=makeQuery(id+"F1.imprint","INTERSECT",VERTEX,{"derivedFrom":[subQ1,subQ0]});Q48=makeQuery(id+"F1.imprint","IMPRINT",FACE,{"disambiguationData":[TD([[makeQuery(id+"F1.imprint","IMPRINT",EDGE,{"disambiguationData":[TD([[subQ2,-1.0]])],"derivedFrom":subQ1}),1.0]])]});}
            var Q49;
            {var subQ0=sQuery(id+"F1.wireOp",EDGE,"E123.trimOffspring");Q49=makeQuery(id+"F1.imprint","IMPRINT",FACE,{"disambiguationData":[TD([[makeQuery(id+"F1.imprint","IMPRINT",EDGE,{"derivedFrom":subQ0}),-1.0]])]});}
            var Q50;
            {var subQ0=sQuery(id+"F1.wireOp",EDGE,"E84");var subQ1=sQuery(id+"F1.wireOp",EDGE,"E43.0");var subQ2=makeQuery(id+"F1.imprint","INTERSECT",VERTEX,{"derivedFrom":[subQ1,subQ0]});Q50=makeQuery(id+"F1.imprint","IMPRINT",FACE,{"disambiguationData":[TD([[makeQuery(id+"F1.imprint","IMPRINT",EDGE,{"disambiguationData":[TD([[subQ2,-1.0]])],"derivedFrom":subQ1}),-1.0]])]});}
            var Q51;
            {var subQ0=sQuery(id+"F1.wireOp",EDGE,"E84");var subQ1=sQuery(id+"F1.wireOp",EDGE,"E32.0");var subQ2=makeQuery(id+"F1.imprint","INTERSECT",VERTEX,{"derivedFrom":[subQ1,subQ0]});Q51=makeQuery(id+"F1.imprint","IMPRINT",FACE,{"disambiguationData":[TD([[makeQuery(id+"F1.imprint","IMPRINT",EDGE,{"disambiguationData":[TD([[subQ2,-1.0]])],"derivedFrom":subQ1}),1.0]])]});}
            var Q52;
            {var subQ0=sQuery(id+"F1.wireOp",EDGE,"E133.trimOffspring");Q52=makeQuery(id+"F1.imprint","IMPRINT",FACE,{"disambiguationData":[TD([[makeQuery(id+"F1.imprint","IMPRINT",EDGE,{"derivedFrom":subQ0}),1.0]])]});}
            var Q53;
            {var subQ0=sQuery(id+"F1.wireOp",EDGE,"E84");var subQ1=sQuery(id+"F1.wireOp",EDGE,"E37.0");var subQ2=makeQuery(id+"F1.imprint","INTERSECT",VERTEX,{"derivedFrom":[subQ1,subQ0]});Q53=makeQuery(id+"F1.imprint","IMPRINT",FACE,{"disambiguationData":[TD([[makeQuery(id+"F1.imprint","IMPRINT",EDGE,{"disambiguationData":[TD([[subQ2,-1.0]])],"derivedFrom":subQ1}),1.0]])]});}
            var Q54;
            {var subQ0=sQuery(id+"F1.wireOp",EDGE,"E141");Q54=makeQuery(id+"F1.imprint","IMPRINT",FACE,{"disambiguationData":[TD([[makeQuery(id+"F1.imprint","IMPRINT",EDGE,{"derivedFrom":subQ0}),1.0]])]});}
            var Q55;
            {var subQ0=sQuery(id+"F1.wireOp",EDGE,"E84");var subQ1=sQuery(id+"F1.wireOp",EDGE,"E17.0");var subQ2=makeQuery(id+"F1.imprint","INTERSECT",VERTEX,{"derivedFrom":[subQ1,subQ0]});Q55=makeQuery(id+"F1.imprint","IMPRINT",FACE,{"disambiguationData":[TD([[makeQuery(id+"F1.imprint","IMPRINT",EDGE,{"disambiguationData":[TD([[subQ2,-1.0]])],"derivedFrom":subQ1}),1.0]])]});}
            var Q56;
            {var subQ0=sQuery(id+"F1.wireOp",EDGE,"E127.trimOffspring");Q56=makeQuery(id+"F1.imprint","IMPRINT",FACE,{"disambiguationData":[TD([[makeQuery(id+"F1.imprint","IMPRINT",EDGE,{"derivedFrom":subQ0}),1.0]])]});}
            var Q57;
            {var subQ0=sQuery(id+"F1.wireOp",EDGE,"E84");var subQ1=sQuery(id+"F1.wireOp",EDGE,"E8.0");var subQ2=makeQuery(id+"F1.imprint","INTERSECT",VERTEX,{"derivedFrom":[subQ1,subQ0]});Q57=makeQuery(id+"F1.imprint","IMPRINT",FACE,{"disambiguationData":[TD([[makeQuery(id+"F1.imprint","IMPRINT",EDGE,{"disambiguationData":[TD([[subQ2,-1.0]])],"derivedFrom":subQ1}),-1.0]])]});}
            var Q58;
            {var subQ0=sQuery(id+"F1.wireOp",EDGE,"E84");var subQ1=sQuery(id+"F1.wireOp",EDGE,"E35.0");var subQ2=makeQuery(id+"F1.imprint","INTERSECT",VERTEX,{"derivedFrom":[subQ1,subQ0]});Q58=makeQuery(id+"F1.imprint","IMPRINT",FACE,{"disambiguationData":[TD([[makeQuery(id+"F1.imprint","IMPRINT",EDGE,{"disambiguationData":[TD([[subQ2,-1.0]])],"derivedFrom":subQ1}),1.0]])]});}
            var Q59;
            {var subQ0=sQuery(id+"F1.wireOp",EDGE,"E84");var subQ1=sQuery(id+"F1.wireOp",EDGE,"E27.0");var subQ2=makeQuery(id+"F1.imprint","INTERSECT",VERTEX,{"derivedFrom":[subQ1,subQ0]});Q59=makeQuery(id+"F1.imprint","IMPRINT",FACE,{"disambiguationData":[TD([[makeQuery(id+"F1.imprint","IMPRINT",EDGE,{"disambiguationData":[TD([[subQ2,-1.0]])],"derivedFrom":subQ1}),1.0]])]});}
            var Q60;
            {var subQ0=sQuery(id+"F1.wireOp",EDGE,"E84");var subQ1=sQuery(id+"F1.wireOp",EDGE,"E42.0");var subQ2=makeQuery(id+"F1.imprint","INTERSECT",VERTEX,{"derivedFrom":[subQ1,subQ0]});Q60=makeQuery(id+"F1.imprint","IMPRINT",FACE,{"disambiguationData":[TD([[makeQuery(id+"F1.imprint","IMPRINT",EDGE,{"disambiguationData":[TD([[subQ2,-1.0]])],"derivedFrom":subQ1}),-1.0]])]});}
            var Q61;
            {var subQ0=sQuery(id+"F1.wireOp",EDGE,"E93.trimOffspring");Q61=makeQuery(id+"F1.imprint","IMPRINT",FACE,{"disambiguationData":[TD([[makeQuery(id+"F1.imprint","IMPRINT",EDGE,{"derivedFrom":subQ0}),-1.0]])]});}
            var Q62;
            {var subQ0=sQuery(id+"F1.wireOp",EDGE,"E84");var subQ1=sQuery(id+"F1.wireOp",EDGE,"E28.0");var subQ2=makeQuery(id+"F1.imprint","INTERSECT",VERTEX,{"derivedFrom":[subQ1,subQ0]});Q62=makeQuery(id+"F1.imprint","IMPRINT",FACE,{"disambiguationData":[TD([[makeQuery(id+"F1.imprint","IMPRINT",EDGE,{"disambiguationData":[TD([[subQ2,-1.0]])],"derivedFrom":subQ1}),-1.0]])]});}
            var Q63;
            {var subQ0=sQuery(id+"F1.wireOp",EDGE,"E84");var subQ1=sQuery(id+"F1.wireOp",EDGE,"E12.0");var subQ2=makeQuery(id+"F1.imprint","INTERSECT",VERTEX,{"derivedFrom":[subQ1,subQ0]});Q63=makeQuery(id+"F1.imprint","IMPRINT",FACE,{"disambiguationData":[TD([[makeQuery(id+"F1.imprint","IMPRINT",EDGE,{"disambiguationData":[TD([[subQ2,-1.0]])],"derivedFrom":subQ1}),-1.0]])]});}
            var Q64;
            {var subQ0=sQuery(id+"F1.wireOp",EDGE,"E84");var subQ1=sQuery(id+"F1.wireOp",EDGE,"E26.0");var subQ2=makeQuery(id+"F1.imprint","INTERSECT",VERTEX,{"derivedFrom":[subQ1,subQ0]});Q64=makeQuery(id+"F1.imprint","IMPRINT",FACE,{"disambiguationData":[TD([[makeQuery(id+"F1.imprint","IMPRINT",EDGE,{"disambiguationData":[TD([[subQ2,-1.0]])],"derivedFrom":subQ1}),1.0]])]});}
            var Q65;
            {var subQ0=sQuery(id+"F1.wireOp",EDGE,"E148.trimOffspring");Q65=makeQuery(id+"F1.imprint","IMPRINT",FACE,{"disambiguationData":[TD([[makeQuery(id+"F1.imprint","IMPRINT",EDGE,{"derivedFrom":subQ0}),1.0]])]});}
            var Q66;
            {var subQ0=sQuery(id+"F1.wireOp",EDGE,"E142.trimOffspring");Q66=makeQuery(id+"F1.imprint","IMPRINT",FACE,{"disambiguationData":[TD([[makeQuery(id+"F1.imprint","IMPRINT",EDGE,{"derivedFrom":subQ0}),1.0]])]});}
            var Q67;
            {var subQ0=sQuery(id+"F1.wireOp",EDGE,"E106.trimOffspring");Q67=makeQuery(id+"F1.imprint","IMPRINT",FACE,{"disambiguationData":[TD([[makeQuery(id+"F1.imprint","IMPRINT",EDGE,{"derivedFrom":subQ0}),-1.0]])]});}
            var Q68;
            {var subQ0=sQuery(id+"F1.wireOp",EDGE,"E84");var subQ1=sQuery(id+"F1.wireOp",EDGE,"E28.0");var subQ2=makeQuery(id+"F1.imprint","INTERSECT",VERTEX,{"derivedFrom":[subQ1,subQ0]});Q68=makeQuery(id+"F1.imprint","IMPRINT",FACE,{"disambiguationData":[TD([[makeQuery(id+"F1.imprint","IMPRINT",EDGE,{"disambiguationData":[TD([[subQ2,-1.0]])],"derivedFrom":subQ1}),1.0]])]});}
            var Q69;
            {var subQ0=sQuery(id+"F1.wireOp",EDGE,"E92.trimOffspring");Q69=makeQuery(id+"F1.imprint","IMPRINT",FACE,{"disambiguationData":[TD([[makeQuery(id+"F1.imprint","IMPRINT",EDGE,{"derivedFrom":subQ0}),-1.0]])]});}
            var Q70;
            {var subQ0=sQuery(id+"F1.wireOp",EDGE,"E84");var subQ1=sQuery(id+"F1.wireOp",EDGE,"E7.0");var subQ2=makeQuery(id+"F1.imprint","INTERSECT",VERTEX,{"derivedFrom":[subQ1,subQ0]});Q70=makeQuery(id+"F1.imprint","IMPRINT",FACE,{"disambiguationData":[TD([[makeQuery(id+"F1.imprint","IMPRINT",EDGE,{"disambiguationData":[TD([[subQ2,-1.0]])],"derivedFrom":subQ1}),-1.0]])]});}
            var Q71;
            {var subQ0=sQuery(id+"F1.wireOp",EDGE,"E84");var subQ1=sQuery(id+"F1.wireOp",EDGE,"E31.0");var subQ2=makeQuery(id+"F1.imprint","INTERSECT",VERTEX,{"derivedFrom":[subQ1,subQ0]});Q71=makeQuery(id+"F1.imprint","IMPRINT",FACE,{"disambiguationData":[TD([[makeQuery(id+"F1.imprint","IMPRINT",EDGE,{"disambiguationData":[TD([[subQ2,-1.0]])],"derivedFrom":subQ1}),1.0]])]});}
            var Q72;
            {var subQ0=sQuery(id+"F1.wireOp",EDGE,"E152");Q72=makeQuery(id+"F1.imprint","IMPRINT",FACE,{"disambiguationData":[TD([[makeQuery(id+"F1.imprint","IMPRINT",EDGE,{"derivedFrom":subQ0}),1.0]])]});}
            var Q73;
            {var subQ0=sQuery(id+"F1.wireOp",EDGE,"E87.trimOffspring");Q73=makeQuery(id+"F1.imprint","IMPRINT",FACE,{"disambiguationData":[TD([[makeQuery(id+"F1.imprint","IMPRINT",EDGE,{"derivedFrom":subQ0}),-1.0]])]});}
            var Q74;
            {var subQ0=sQuery(id+"F1.wireOp",EDGE,"E84");var subQ1=sQuery(id+"F1.wireOp",EDGE,"E22.0");var subQ2=makeQuery(id+"F1.imprint","INTERSECT",VERTEX,{"derivedFrom":[subQ1,subQ0]});Q74=makeQuery(id+"F1.imprint","IMPRINT",FACE,{"disambiguationData":[TD([[makeQuery(id+"F1.imprint","IMPRINT",EDGE,{"disambiguationData":[TD([[subQ2,-1.0]])],"derivedFrom":subQ1}),-1.0]])]});}
            var Q75;
            {var subQ0=sQuery(id+"F1.wireOp",EDGE,"E84");var subQ1=sQuery(id+"F1.wireOp",EDGE,"E44.0");var subQ2=makeQuery(id+"F1.imprint","INTERSECT",VERTEX,{"derivedFrom":[subQ1,subQ0]});Q75=makeQuery(id+"F1.imprint","IMPRINT",FACE,{"disambiguationData":[TD([[makeQuery(id+"F1.imprint","IMPRINT",EDGE,{"disambiguationData":[TD([[subQ2,-1.0]])],"derivedFrom":subQ1}),1.0]])]});}
            var Q76;
            {var subQ0=sQuery(id+"F1.wireOp",EDGE,"E84");var subQ1=sQuery(id+"F1.wireOp",EDGE,"E18.0");var subQ2=makeQuery(id+"F1.imprint","INTERSECT",VERTEX,{"derivedFrom":[subQ1,subQ0]});Q76=makeQuery(id+"F1.imprint","IMPRINT",FACE,{"disambiguationData":[TD([[makeQuery(id+"F1.imprint","IMPRINT",EDGE,{"disambiguationData":[TD([[subQ2,-1.0]])],"derivedFrom":subQ1}),1.0]])]});}
            var Q77;
            {var subQ0=sQuery(id+"F1.wireOp",EDGE,"E96.trimOffspring");Q77=makeQuery(id+"F1.imprint","IMPRINT",FACE,{"disambiguationData":[TD([[makeQuery(id+"F1.imprint","IMPRINT",EDGE,{"derivedFrom":subQ0}),-1.0]])]});}
            var Q78;
            {var subQ0=sQuery(id+"F1.wireOp",EDGE,"E139.trimOffspring");Q78=makeQuery(id+"F1.imprint","IMPRINT",FACE,{"disambiguationData":[TD([[makeQuery(id+"F1.imprint","IMPRINT",EDGE,{"derivedFrom":subQ0}),1.0]])]});}
            var Q79;
            {var subQ0=sQuery(id+"F1.wireOp",EDGE,"E84");var subQ1=sQuery(id+"F1.wireOp",EDGE,"E7.0");var subQ2=makeQuery(id+"F1.imprint","INTERSECT",VERTEX,{"derivedFrom":[subQ1,subQ0]});Q79=makeQuery(id+"F1.imprint","IMPRINT",FACE,{"disambiguationData":[TD([[makeQuery(id+"F1.imprint","IMPRINT",EDGE,{"disambiguationData":[TD([[subQ2,-1.0]])],"derivedFrom":subQ1}),1.0]])]});}
            var Q80;
            {var subQ0=sQuery(id+"F1.wireOp",EDGE,"E84");var subQ1=sQuery(id+"F1.wireOp",EDGE,"E30.0");var subQ2=makeQuery(id+"F1.imprint","INTERSECT",VERTEX,{"derivedFrom":[subQ1,subQ0]});Q80=makeQuery(id+"F1.imprint","IMPRINT",FACE,{"disambiguationData":[TD([[makeQuery(id+"F1.imprint","IMPRINT",EDGE,{"disambiguationData":[TD([[subQ2,-1.0]])],"derivedFrom":subQ1}),1.0]])]});}
            var Q81;
            {var subQ0=sQuery(id+"F1.wireOp",EDGE,"E125.trimOffspring");Q81=makeQuery(id+"F1.imprint","IMPRINT",FACE,{"disambiguationData":[TD([[makeQuery(id+"F1.imprint","IMPRINT",EDGE,{"derivedFrom":subQ0}),1.0]])]});}
            var Q82;
            {var subQ0=sQuery(id+"F1.wireOp",EDGE,"E124.trimOffspring");Q82=makeQuery(id+"F1.imprint","IMPRINT",FACE,{"disambiguationData":[TD([[makeQuery(id+"F1.imprint","IMPRINT",EDGE,{"derivedFrom":subQ0}),-1.0]])]});}
            var Q83;
            {var subQ0=sQuery(id+"F1.wireOp",EDGE,"E84");var subQ1=sQuery(id+"F1.wireOp",EDGE,"E27.0");var subQ2=makeQuery(id+"F1.imprint","INTERSECT",VERTEX,{"derivedFrom":[subQ1,subQ0]});Q83=makeQuery(id+"F1.imprint","IMPRINT",FACE,{"disambiguationData":[TD([[makeQuery(id+"F1.imprint","IMPRINT",EDGE,{"disambiguationData":[TD([[subQ2,-1.0]])],"derivedFrom":subQ1}),-1.0]])]});}
            var Q84;
            {var subQ0=sQuery(id+"F1.wireOp",EDGE,"E147.trimOffspring");Q84=makeQuery(id+"F1.imprint","IMPRINT",FACE,{"disambiguationData":[TD([[makeQuery(id+"F1.imprint","IMPRINT",EDGE,{"derivedFrom":subQ0}),1.0]])]});}
            var Q85;
            {var subQ0=sQuery(id+"F1.wireOp",EDGE,"E84");var subQ1=sQuery(id+"F1.wireOp",EDGE,"E37.0");var subQ2=makeQuery(id+"F1.imprint","INTERSECT",VERTEX,{"derivedFrom":[subQ1,subQ0]});Q85=makeQuery(id+"F1.imprint","IMPRINT",FACE,{"disambiguationData":[TD([[makeQuery(id+"F1.imprint","IMPRINT",EDGE,{"disambiguationData":[TD([[subQ2,-1.0]])],"derivedFrom":subQ1}),-1.0]])]});}
            var Q86;
            {var subQ0=sQuery(id+"F1.wireOp",EDGE,"E84");var subQ1=sQuery(id+"F1.wireOp",EDGE,"E32.0");var subQ2=makeQuery(id+"F1.imprint","INTERSECT",VERTEX,{"derivedFrom":[subQ1,subQ0]});Q86=makeQuery(id+"F1.imprint","IMPRINT",FACE,{"disambiguationData":[TD([[makeQuery(id+"F1.imprint","IMPRINT",EDGE,{"disambiguationData":[TD([[subQ2,-1.0]])],"derivedFrom":subQ1}),-1.0]])]});}
            var Q87;
            {var subQ0=sQuery(id+"F1.wireOp",EDGE,"E131");Q87=makeQuery(id+"F1.imprint","IMPRINT",FACE,{"disambiguationData":[TD([[makeQuery(id+"F1.imprint","IMPRINT",EDGE,{"derivedFrom":subQ0}),1.0]])]});}
            var Q88;
            {var subQ0=sQuery(id+"F1.wireOp",EDGE,"E84");var subQ1=sQuery(id+"F1.wireOp",EDGE,"E34.0");var subQ2=makeQuery(id+"F1.imprint","INTERSECT",VERTEX,{"derivedFrom":[subQ1,subQ0]});Q88=makeQuery(id+"F1.imprint","IMPRINT",FACE,{"disambiguationData":[TD([[makeQuery(id+"F1.imprint","IMPRINT",EDGE,{"disambiguationData":[TD([[subQ2,-1.0]])],"derivedFrom":subQ1}),-1.0]])]});}
            var Q89;
            {var subQ0=sQuery(id+"F1.wireOp",EDGE,"E84");var subQ1=sQuery(id+"F1.wireOp",EDGE,"E14.0");var subQ2=makeQuery(id+"F1.imprint","INTERSECT",VERTEX,{"derivedFrom":[subQ1,subQ0]});Q89=makeQuery(id+"F1.imprint","IMPRINT",FACE,{"disambiguationData":[TD([[makeQuery(id+"F1.imprint","IMPRINT",EDGE,{"disambiguationData":[TD([[subQ2,-1.0]])],"derivedFrom":subQ1}),1.0]])]});}
            var Q90;
            {var subQ0=sQuery(id+"F1.wireOp",EDGE,"E145.trimOffspring");Q90=makeQuery(id+"F1.imprint","IMPRINT",FACE,{"disambiguationData":[TD([[makeQuery(id+"F1.imprint","IMPRINT",EDGE,{"derivedFrom":subQ0}),1.0]])]});}
            var Q91;
            {var subQ0=sQuery(id+"F1.wireOp",EDGE,"E84");var subQ1=sQuery(id+"F1.wireOp",EDGE,"E44.0");var subQ2=makeQuery(id+"F1.imprint","INTERSECT",VERTEX,{"derivedFrom":[subQ1,subQ0]});Q91=makeQuery(id+"F1.imprint","IMPRINT",FACE,{"disambiguationData":[TD([[makeQuery(id+"F1.imprint","IMPRINT",EDGE,{"disambiguationData":[TD([[subQ2,-1.0]])],"derivedFrom":subQ1}),-1.0]])]});}
            var Q92;
            {var subQ0=sQuery(id+"F1.wireOp",EDGE,"E101.trimOffspring");Q92=makeQuery(id+"F1.imprint","IMPRINT",FACE,{"disambiguationData":[TD([[makeQuery(id+"F1.imprint","IMPRINT",EDGE,{"derivedFrom":subQ0}),-1.0]])]});}
            var Q93;
            {var subQ0=sQuery(id+"F1.wireOp",EDGE,"E84");var subQ1=sQuery(id+"F1.wireOp",EDGE,"E20.0");var subQ2=makeQuery(id+"F1.imprint","INTERSECT",VERTEX,{"derivedFrom":[subQ1,subQ0]});Q93=makeQuery(id+"F1.imprint","IMPRINT",FACE,{"disambiguationData":[TD([[makeQuery(id+"F1.imprint","IMPRINT",EDGE,{"disambiguationData":[TD([[subQ2,-1.0]])],"derivedFrom":subQ1}),-1.0]])]});}
            var Q94;
            {var subQ0=sQuery(id+"F1.wireOp",EDGE,"E89.trimOffspring");Q94=makeQuery(id+"F1.imprint","IMPRINT",FACE,{"disambiguationData":[TD([[makeQuery(id+"F1.imprint","IMPRINT",EDGE,{"derivedFrom":subQ0}),-1.0]])]});}
            var Q95;
            {var subQ0=sQuery(id+"F1.wireOp",EDGE,"E84");var subQ1=sQuery(id+"F1.wireOp",EDGE,"E36.0");var subQ2=makeQuery(id+"F1.imprint","INTERSECT",VERTEX,{"derivedFrom":[subQ1,subQ0]});Q95=makeQuery(id+"F1.imprint","IMPRINT",FACE,{"disambiguationData":[TD([[makeQuery(id+"F1.imprint","IMPRINT",EDGE,{"disambiguationData":[TD([[subQ2,-1.0]])],"derivedFrom":subQ1}),-1.0]])]});}
            var Q96;
            {var subQ0=sQuery(id+"F1.wireOp",EDGE,"E150.trimOffspring");Q96=makeQuery(id+"F1.imprint","IMPRINT",FACE,{"disambiguationData":[TD([[makeQuery(id+"F1.imprint","IMPRINT",EDGE,{"derivedFrom":subQ0}),1.0]])]});}
            var Q97;
            {var subQ0=sQuery(id+"F1.wireOp",EDGE,"E84");var subQ1=sQuery(id+"F1.wireOp",EDGE,"E34.0");var subQ2=makeQuery(id+"F1.imprint","INTERSECT",VERTEX,{"derivedFrom":[subQ1,subQ0]});Q97=makeQuery(id+"F1.imprint","IMPRINT",FACE,{"disambiguationData":[TD([[makeQuery(id+"F1.imprint","IMPRINT",EDGE,{"disambiguationData":[TD([[subQ2,-1.0]])],"derivedFrom":subQ1}),1.0]])]});}
            var Q98;
            {var subQ0=sQuery(id+"F1.wireOp",EDGE,"E103.trimOffspring");Q98=makeQuery(id+"F1.imprint","IMPRINT",FACE,{"disambiguationData":[TD([[makeQuery(id+"F1.imprint","IMPRINT",EDGE,{"derivedFrom":subQ0}),-1.0]])]});}
            var Q99;
            {var subQ0=sQuery(id+"F1.wireOp",EDGE,"E84");var subQ1=sQuery(id+"F1.wireOp",EDGE,"E16.0");var subQ2=makeQuery(id+"F1.imprint","INTERSECT",VERTEX,{"derivedFrom":[subQ1,subQ0]});Q99=makeQuery(id+"F1.imprint","IMPRINT",FACE,{"disambiguationData":[TD([[makeQuery(id+"F1.imprint","IMPRINT",EDGE,{"disambiguationData":[TD([[subQ2,-1.0]])],"derivedFrom":subQ1}),-1.0]])]});}
            var Q100;
            {var subQ0=sQuery(id+"F1.wireOp",EDGE,"E109.trimOffspring");Q100=makeQuery(id+"F1.imprint","IMPRINT",FACE,{"disambiguationData":[TD([[makeQuery(id+"F1.imprint","IMPRINT",EDGE,{"derivedFrom":subQ0}),-1.0]])]});}
            var Q101;
            {var subQ0=sQuery(id+"F1.wireOp",EDGE,"E155.trimOffspring");Q101=makeQuery(id+"F1.imprint","IMPRINT",FACE,{"disambiguationData":[TD([[makeQuery(id+"F1.imprint","IMPRINT",EDGE,{"derivedFrom":subQ0}),1.0]])]});}
            var Q102;
            {var subQ0=sQuery(id+"F1.wireOp",EDGE,"E90.trimOffspring");Q102=makeQuery(id+"F1.imprint","IMPRINT",FACE,{"disambiguationData":[TD([[makeQuery(id+"F1.imprint","IMPRINT",EDGE,{"derivedFrom":subQ0}),-1.0]])]});}
            var Q103;
            {var subQ0=sQuery(id+"F1.wireOp",EDGE,"E128.trimOffspring");Q103=makeQuery(id+"F1.imprint","IMPRINT",FACE,{"disambiguationData":[TD([[makeQuery(id+"F1.imprint","IMPRINT",EDGE,{"derivedFrom":subQ0}),1.0]])]});}
            var Q104;
            {var subQ0=sQuery(id+"F1.wireOp",EDGE,"E84");var subQ1=sQuery(id+"F1.wireOp",EDGE,"E23.0");var subQ2=makeQuery(id+"F1.imprint","INTERSECT",VERTEX,{"derivedFrom":[subQ1,subQ0]});Q104=makeQuery(id+"F1.imprint","IMPRINT",FACE,{"disambiguationData":[TD([[makeQuery(id+"F1.imprint","IMPRINT",EDGE,{"disambiguationData":[TD([[subQ2,-1.0]])],"derivedFrom":subQ1}),-1.0]])]});}
            var Q105;
            {var subQ0=sQuery(id+"F1.wireOp",EDGE,"E84");var subQ1=sQuery(id+"F1.wireOp",EDGE,"E42.0");var subQ2=makeQuery(id+"F1.imprint","INTERSECT",VERTEX,{"derivedFrom":[subQ1,subQ0]});Q105=makeQuery(id+"F1.imprint","IMPRINT",FACE,{"disambiguationData":[TD([[makeQuery(id+"F1.imprint","IMPRINT",EDGE,{"disambiguationData":[TD([[subQ2,-1.0]])],"derivedFrom":subQ1}),1.0]])]});}
            var Q106;
            {var subQ0=sQuery(id+"F1.wireOp",EDGE,"E108.trimOffspring");Q106=makeQuery(id+"F1.imprint","IMPRINT",FACE,{"disambiguationData":[TD([[makeQuery(id+"F1.imprint","IMPRINT",EDGE,{"derivedFrom":subQ0}),-1.0]])]});}
            var Q107;
            {var subQ0=sQuery(id+"F1.wireOp",EDGE,"E84");var subQ1=sQuery(id+"F1.wireOp",EDGE,"E29.0");var subQ2=makeQuery(id+"F1.imprint","INTERSECT",VERTEX,{"derivedFrom":[subQ1,subQ0]});Q107=makeQuery(id+"F1.imprint","IMPRINT",FACE,{"disambiguationData":[TD([[makeQuery(id+"F1.imprint","IMPRINT",EDGE,{"disambiguationData":[TD([[subQ2,-1.0]])],"derivedFrom":subQ1}),1.0]])]});}
            var Q108;
            {var subQ0=sQuery(id+"F1.wireOp",EDGE,"E110.trimOffspring");Q108=makeQuery(id+"F1.imprint","IMPRINT",FACE,{"disambiguationData":[TD([[makeQuery(id+"F1.imprint","IMPRINT",EDGE,{"derivedFrom":subQ0}),-1.0]])]});}
            var Q109;
            {var subQ0=sQuery(id+"F1.wireOp",EDGE,"E159");Q109=makeQuery(id+"F1.imprint","IMPRINT",FACE,{"disambiguationData":[TD([[makeQuery(id+"F1.imprint","IMPRINT",EDGE,{"derivedFrom":subQ0}),1.0]])]});}
            var Q110;
            {var subQ0=sQuery(id+"F1.wireOp",EDGE,"E119.trimOffspring");Q110=makeQuery(id+"F1.imprint","IMPRINT",FACE,{"disambiguationData":[TD([[makeQuery(id+"F1.imprint","IMPRINT",EDGE,{"derivedFrom":subQ0}),-1.0]])]});}
            var Q111;
            {var subQ0=sQuery(id+"F1.wireOp",EDGE,"E84");var subQ1=sQuery(id+"F1.wireOp",EDGE,"E24.0");var subQ2=makeQuery(id+"F1.imprint","INTERSECT",VERTEX,{"derivedFrom":[subQ1,subQ0]});Q111=makeQuery(id+"F1.imprint","IMPRINT",FACE,{"disambiguationData":[TD([[makeQuery(id+"F1.imprint","IMPRINT",EDGE,{"disambiguationData":[TD([[subQ2,-1.0]])],"derivedFrom":subQ1}),-1.0]])]});}
            var Q112;
            {var subQ0=sQuery(id+"F1.wireOp",EDGE,"E97.trimOffspring");Q112=makeQuery(id+"F1.imprint","IMPRINT",FACE,{"disambiguationData":[TD([[makeQuery(id+"F1.imprint","IMPRINT",EDGE,{"derivedFrom":subQ0}),-1.0]])]});}
            var Q113;
            {var subQ0=sQuery(id+"F1.wireOp",EDGE,"E84");var subQ1=sQuery(id+"F1.wireOp",EDGE,"E23.0");var subQ2=makeQuery(id+"F1.imprint","INTERSECT",VERTEX,{"derivedFrom":[subQ1,subQ0]});Q113=makeQuery(id+"F1.imprint","IMPRINT",FACE,{"disambiguationData":[TD([[makeQuery(id+"F1.imprint","IMPRINT",EDGE,{"disambiguationData":[TD([[subQ2,-1.0]])],"derivedFrom":subQ1}),1.0]])]});}
            var Q114;
            {var subQ0=sQuery(id+"F1.wireOp",EDGE,"E132");Q114=makeQuery(id+"F1.imprint","IMPRINT",FACE,{"disambiguationData":[TD([[makeQuery(id+"F1.imprint","IMPRINT",EDGE,{"derivedFrom":subQ0}),1.0]])]});}
            var Q115;
            {var subQ0=sQuery(id+"F1.wireOp",EDGE,"E84");var subQ1=sQuery(id+"F1.wireOp",EDGE,"E8.0");var subQ2=makeQuery(id+"F1.imprint","INTERSECT",VERTEX,{"derivedFrom":[subQ1,subQ0]});Q115=makeQuery(id+"F1.imprint","IMPRINT",FACE,{"disambiguationData":[TD([[makeQuery(id+"F1.imprint","IMPRINT",EDGE,{"disambiguationData":[TD([[subQ2,-1.0]])],"derivedFrom":subQ1}),1.0]])]});}
            var Q116;
            {var subQ0=sQuery(id+"F1.wireOp",EDGE,"E84");var subQ1=sQuery(id+"F1.wireOp",EDGE,"E16.0");var subQ2=makeQuery(id+"F1.imprint","INTERSECT",VERTEX,{"derivedFrom":[subQ1,subQ0]});Q116=makeQuery(id+"F1.imprint","IMPRINT",FACE,{"disambiguationData":[TD([[makeQuery(id+"F1.imprint","IMPRINT",EDGE,{"disambiguationData":[TD([[subQ2,-1.0]])],"derivedFrom":subQ1}),1.0]])]});}
            var Q117;
            {var subQ0=sQuery(id+"F1.wireOp",EDGE,"E84");var subQ1=sQuery(id+"F1.wireOp",EDGE,"E15.0");var subQ2=makeQuery(id+"F1.imprint","INTERSECT",VERTEX,{"derivedFrom":[subQ1,subQ0]});Q117=makeQuery(id+"F1.imprint","IMPRINT",FACE,{"disambiguationData":[TD([[makeQuery(id+"F1.imprint","IMPRINT",EDGE,{"disambiguationData":[TD([[subQ2,-1.0]])],"derivedFrom":subQ1}),1.0]])]});}
            var Q118;
            {var subQ0=sQuery(id+"F1.wireOp",EDGE,"E84");var subQ1=sQuery(id+"F1.wireOp",EDGE,"E41.0");var subQ2=makeQuery(id+"F1.imprint","INTERSECT",VERTEX,{"derivedFrom":[subQ1,subQ0]});Q118=makeQuery(id+"F1.imprint","IMPRINT",FACE,{"disambiguationData":[TD([[makeQuery(id+"F1.imprint","IMPRINT",EDGE,{"disambiguationData":[TD([[subQ2,-1.0]])],"derivedFrom":subQ1}),-1.0]])]});}
            var Q119;
            {var subQ0=sQuery(id+"F1.wireOp",EDGE,"E157.trimOffspring");Q119=makeQuery(id+"F1.imprint","IMPRINT",FACE,{"disambiguationData":[TD([[makeQuery(id+"F1.imprint","IMPRINT",EDGE,{"derivedFrom":subQ0}),1.0]])]});}
            var Q120;
            {var subQ0=sQuery(id+"F1.wireOp",EDGE,"E84");var subQ1=sQuery(id+"F1.wireOp",EDGE,"E6.0");var subQ2=makeQuery(id+"F1.imprint","INTERSECT",VERTEX,{"derivedFrom":[subQ1,subQ0]});Q120=makeQuery(id+"F1.imprint","IMPRINT",FACE,{"disambiguationData":[TD([[makeQuery(id+"F1.imprint","IMPRINT",EDGE,{"disambiguationData":[TD([[subQ2,-1.0]])],"derivedFrom":subQ1}),1.0]])]});}
            var Q121;
            {var subQ0=sQuery(id+"F1.wireOp",EDGE,"E104.trimOffspring");Q121=makeQuery(id+"F1.imprint","IMPRINT",FACE,{"disambiguationData":[TD([[makeQuery(id+"F1.imprint","IMPRINT",EDGE,{"derivedFrom":subQ0}),-1.0]])]});}
            var Q122;
            {var subQ0=sQuery(id+"F1.wireOp",EDGE,"E94.trimOffspring");Q122=makeQuery(id+"F1.imprint","IMPRINT",FACE,{"disambiguationData":[TD([[makeQuery(id+"F1.imprint","IMPRINT",EDGE,{"derivedFrom":subQ0}),-1.0]])]});}
            var Q123;
            {var subQ0=sQuery(id+"F1.wireOp",EDGE,"E84");var subQ1=sQuery(id+"F1.wireOp",EDGE,"E11.0");var subQ2=makeQuery(id+"F1.imprint","INTERSECT",VERTEX,{"derivedFrom":[subQ1,subQ0]});Q123=makeQuery(id+"F1.imprint","IMPRINT",FACE,{"disambiguationData":[TD([[makeQuery(id+"F1.imprint","IMPRINT",EDGE,{"disambiguationData":[TD([[subQ2,-1.0]])],"derivedFrom":subQ1}),-1.0]])]});}
            var Q124;
            {var subQ0=sQuery(id+"F1.wireOp",EDGE,"E84");var subQ1=sQuery(id+"F1.wireOp",EDGE,"E38.0");var subQ2=makeQuery(id+"F1.imprint","INTERSECT",VERTEX,{"derivedFrom":[subQ1,subQ0]});Q124=makeQuery(id+"F1.imprint","IMPRINT",FACE,{"disambiguationData":[TD([[makeQuery(id+"F1.imprint","IMPRINT",EDGE,{"disambiguationData":[TD([[subQ2,-1.0]])],"derivedFrom":subQ1}),-1.0]])]});}
            var Q125;
            {var subQ0=sQuery(id+"F1.wireOp",EDGE,"E84");var subQ1=sQuery(id+"F1.wireOp",EDGE,"E10.0");var subQ2=makeQuery(id+"F1.imprint","INTERSECT",VERTEX,{"derivedFrom":[subQ1,subQ0]});Q125=makeQuery(id+"F1.imprint","IMPRINT",FACE,{"disambiguationData":[TD([[makeQuery(id+"F1.imprint","IMPRINT",EDGE,{"disambiguationData":[TD([[subQ2,-1.0]])],"derivedFrom":subQ1}),1.0]])]});}
            var Q126;
            {var subQ0=sQuery(id+"F1.wireOp",EDGE,"E111.trimOffspring");Q126=makeQuery(id+"F1.imprint","IMPRINT",FACE,{"disambiguationData":[TD([[makeQuery(id+"F1.imprint","IMPRINT",EDGE,{"derivedFrom":subQ0}),-1.0]])]});}
            var Q127;
            {var subQ0=sQuery(id+"F1.wireOp",EDGE,"E144.trimOffspring");Q127=makeQuery(id+"F1.imprint","IMPRINT",FACE,{"disambiguationData":[TD([[makeQuery(id+"F1.imprint","IMPRINT",EDGE,{"derivedFrom":subQ0}),1.0]])]});}
            var Q128;
            {var subQ0=sQuery(id+"F1.wireOp",EDGE,"E135.trimOffspring");Q128=makeQuery(id+"F1.imprint","IMPRINT",FACE,{"disambiguationData":[TD([[makeQuery(id+"F1.imprint","IMPRINT",EDGE,{"derivedFrom":subQ0}),1.0]])]});}
            var Q129;
            {var subQ0=sQuery(id+"F1.wireOp",EDGE,"E84");var subQ1=sQuery(id+"F1.wireOp",EDGE,"E13.0");var subQ2=makeQuery(id+"F1.imprint","INTERSECT",VERTEX,{"derivedFrom":[subQ1,subQ0]});Q129=makeQuery(id+"F1.imprint","IMPRINT",FACE,{"disambiguationData":[TD([[makeQuery(id+"F1.imprint","IMPRINT",EDGE,{"disambiguationData":[TD([[subQ2,-1.0]])],"derivedFrom":subQ1}),1.0]])]});}
            var Q130;
            {var subQ0=sQuery(id+"F1.wireOp",EDGE,"E84");var subQ1=sQuery(id+"F1.wireOp",EDGE,"E25.0");var subQ2=makeQuery(id+"F1.imprint","INTERSECT",VERTEX,{"derivedFrom":[subQ1,subQ0]});Q130=makeQuery(id+"F1.imprint","IMPRINT",FACE,{"disambiguationData":[TD([[makeQuery(id+"F1.imprint","IMPRINT",EDGE,{"disambiguationData":[TD([[subQ2,-1.0]])],"derivedFrom":subQ1}),1.0]])]});}
            var Q131;
            {var subQ0=sQuery(id+"F1.wireOp",EDGE,"E162");Q131=makeQuery(id+"F1.imprint","IMPRINT",FACE,{"disambiguationData":[TD([[makeQuery(id+"F1.imprint","IMPRINT",EDGE,{"derivedFrom":subQ0}),1.0]])]});}
            var Q132;
            {var subQ0=sQuery(id+"F1.wireOp",EDGE,"E137");Q132=makeQuery(id+"F1.imprint","IMPRINT",FACE,{"disambiguationData":[TD([[makeQuery(id+"F1.imprint","IMPRINT",EDGE,{"derivedFrom":subQ0}),1.0]])]});}
            var Q133;
            {var subQ0=sQuery(id+"F1.wireOp",EDGE,"E116.trimOffspring");Q133=makeQuery(id+"F1.imprint","IMPRINT",FACE,{"disambiguationData":[TD([[makeQuery(id+"F1.imprint","IMPRINT",EDGE,{"derivedFrom":subQ0}),-1.0]])]});}
            var Q134;
            {var subQ0=sQuery(id+"F1.wireOp",EDGE,"E126.trimOffspring");Q134=makeQuery(id+"F1.imprint","IMPRINT",FACE,{"disambiguationData":[TD([[makeQuery(id+"F1.imprint","IMPRINT",EDGE,{"derivedFrom":subQ0}),1.0]])]});}
            var Q135;
            {var subQ0=sQuery(id+"F1.wireOp",EDGE,"E84");var subQ1=sQuery(id+"F1.wireOp",EDGE,"E9.0");var subQ2=makeQuery(id+"F1.imprint","INTERSECT",VERTEX,{"derivedFrom":[subQ1,subQ0]});Q135=makeQuery(id+"F1.imprint","IMPRINT",FACE,{"disambiguationData":[TD([[makeQuery(id+"F1.imprint","IMPRINT",EDGE,{"disambiguationData":[TD([[subQ2,-1.0]])],"derivedFrom":subQ1}),1.0]])]});}
            var Q136;
            {var subQ0=sQuery(id+"F1.wireOp",EDGE,"E84");var subQ1=sQuery(id+"F1.wireOp",EDGE,"E40.0");var subQ2=makeQuery(id+"F1.imprint","INTERSECT",VERTEX,{"derivedFrom":[subQ1,subQ0]});Q136=makeQuery(id+"F1.imprint","IMPRINT",FACE,{"disambiguationData":[TD([[makeQuery(id+"F1.imprint","IMPRINT",EDGE,{"disambiguationData":[TD([[subQ2,-1.0]])],"derivedFrom":subQ1}),-1.0]])]});}
            var Q137;
            {var subQ0=sQuery(id+"F1.wireOp",EDGE,"E149.trimOffspring");Q137=makeQuery(id+"F1.imprint","IMPRINT",FACE,{"disambiguationData":[TD([[makeQuery(id+"F1.imprint","IMPRINT",EDGE,{"derivedFrom":subQ0}),1.0]])]});}
            var Q138;
            {var subQ0=sQuery(id+"F1.wireOp",EDGE,"E84");var subQ1=sQuery(id+"F1.wireOp",EDGE,"E25.0");var subQ2=makeQuery(id+"F1.imprint","INTERSECT",VERTEX,{"derivedFrom":[subQ1,subQ0]});Q138=makeQuery(id+"F1.imprint","IMPRINT",FACE,{"disambiguationData":[TD([[makeQuery(id+"F1.imprint","IMPRINT",EDGE,{"disambiguationData":[TD([[subQ2,-1.0]])],"derivedFrom":subQ1}),-1.0]])]});}
            var Q139;
            {var subQ0=sQuery(id+"F1.wireOp",EDGE,"E84");var subQ1=sQuery(id+"F1.wireOp",EDGE,"E41.0");var subQ2=makeQuery(id+"F1.imprint","INTERSECT",VERTEX,{"derivedFrom":[subQ1,subQ0]});Q139=makeQuery(id+"F1.imprint","IMPRINT",FACE,{"disambiguationData":[TD([[makeQuery(id+"F1.imprint","IMPRINT",EDGE,{"disambiguationData":[TD([[subQ2,-1.0]])],"derivedFrom":subQ1}),1.0]])]});}
            var Q140;
            {var subQ0=sQuery(id+"F1.wireOp",EDGE,"E84");var subQ1=sQuery(id+"F1.wireOp",EDGE,"E45.0");var subQ2=makeQuery(id+"F1.imprint","INTERSECT",VERTEX,{"derivedFrom":[subQ1,subQ0]});Q140=makeQuery(id+"F1.imprint","IMPRINT",FACE,{"disambiguationData":[TD([[makeQuery(id+"F1.imprint","IMPRINT",EDGE,{"disambiguationData":[TD([[subQ2,-1.0]])],"derivedFrom":subQ1}),-1.0]])]});}
            var Q141;
            {var subQ0=sQuery(id+"F1.wireOp",EDGE,"E98.trimOffspring");Q141=makeQuery(id+"F1.imprint","IMPRINT",FACE,{"disambiguationData":[TD([[makeQuery(id+"F1.imprint","IMPRINT",EDGE,{"derivedFrom":subQ0}),-1.0]])]});}
            var Q142;
            {var subQ0=sQuery(id+"F1.wireOp",EDGE,"E163");Q142=makeQuery(id+"F1.imprint","IMPRINT",FACE,{"disambiguationData":[TD([[makeQuery(id+"F1.imprint","IMPRINT",EDGE,{"derivedFrom":subQ0}),1.0]])]});}
            var Q143;
            {var subQ0=sQuery(id+"F1.wireOp",EDGE,"E153");Q143=makeQuery(id+"F1.imprint","IMPRINT",FACE,{"disambiguationData":[TD([[makeQuery(id+"F1.imprint","IMPRINT",EDGE,{"derivedFrom":subQ0}),1.0]])]});}
            var Q144;
            {var subQ0=sQuery(id+"F1.wireOp",EDGE,"E113.trimOffspring");Q144=makeQuery(id+"F1.imprint","IMPRINT",FACE,{"disambiguationData":[TD([[makeQuery(id+"F1.imprint","IMPRINT",EDGE,{"derivedFrom":subQ0}),-1.0]])]});}
            var Q145;
            {var subQ0=sQuery(id+"F1.wireOp",EDGE,"E84");var subQ1=sQuery(id+"F1.wireOp",EDGE,"E22.0");var subQ2=makeQuery(id+"F1.imprint","INTERSECT",VERTEX,{"derivedFrom":[subQ1,subQ0]});Q145=makeQuery(id+"F1.imprint","IMPRINT",FACE,{"disambiguationData":[TD([[makeQuery(id+"F1.imprint","IMPRINT",EDGE,{"disambiguationData":[TD([[subQ2,-1.0]])],"derivedFrom":subQ1}),1.0]])]});}
            var Q146;
            {var subQ0=sQuery(id+"F1.wireOp",EDGE,"E84");var subQ1=sQuery(id+"F1.wireOp",EDGE,"E39.0");var subQ2=makeQuery(id+"F1.imprint","INTERSECT",VERTEX,{"derivedFrom":[subQ1,subQ0]});Q146=makeQuery(id+"F1.imprint","IMPRINT",FACE,{"disambiguationData":[TD([[makeQuery(id+"F1.imprint","IMPRINT",EDGE,{"disambiguationData":[TD([[subQ2,-1.0]])],"derivedFrom":subQ1}),-1.0]])]});}
            var Q147;
            {var subQ0=sQuery(id+"F1.wireOp",EDGE,"E84");var subQ1=sQuery(id+"F1.wireOp",EDGE,"E33.0");var subQ2=makeQuery(id+"F1.imprint","INTERSECT",VERTEX,{"derivedFrom":[subQ1,subQ0]});Q147=makeQuery(id+"F1.imprint","IMPRINT",FACE,{"disambiguationData":[TD([[makeQuery(id+"F1.imprint","IMPRINT",EDGE,{"disambiguationData":[TD([[subQ2,-1.0]])],"derivedFrom":subQ1}),1.0]])]});}
            var Q148;
            {var subQ0=sQuery(id+"F1.wireOp",EDGE,"E84");var subQ1=sQuery(id+"F1.wireOp",EDGE,"E5.0");var subQ2=makeQuery(id+"F1.imprint","INTERSECT",VERTEX,{"derivedFrom":[subQ1,subQ0]});Q148=makeQuery(id+"F1.imprint","IMPRINT",FACE,{"disambiguationData":[TD([[makeQuery(id+"F1.imprint","IMPRINT",EDGE,{"disambiguationData":[TD([[subQ2,-1.0]])],"derivedFrom":subQ1}),1.0]])]});}
            var Q149;
            {var subQ0=sQuery(id+"F1.wireOp",EDGE,"E160");Q149=makeQuery(id+"F1.imprint","IMPRINT",FACE,{"disambiguationData":[TD([[makeQuery(id+"F1.imprint","IMPRINT",EDGE,{"derivedFrom":subQ0}),1.0]])]});}
            var Q150;
            {var subQ0=sQuery(id+"F1.wireOp",EDGE,"E84");var subQ1=sQuery(id+"F1.wireOp",EDGE,"E20.0");var subQ2=makeQuery(id+"F1.imprint","INTERSECT",VERTEX,{"derivedFrom":[subQ1,subQ0]});Q150=makeQuery(id+"F1.imprint","IMPRINT",FACE,{"disambiguationData":[TD([[makeQuery(id+"F1.imprint","IMPRINT",EDGE,{"disambiguationData":[TD([[subQ2,-1.0]])],"derivedFrom":subQ1}),1.0]])]});}
            var Q151;
            {var subQ0=sQuery(id+"F1.wireOp",EDGE,"E114.trimOffspring");Q151=makeQuery(id+"F1.imprint","IMPRINT",FACE,{"disambiguationData":[TD([[makeQuery(id+"F1.imprint","IMPRINT",EDGE,{"derivedFrom":subQ0}),-1.0]])]});}
            var Q152;
            {var subQ0=sQuery(id+"F1.wireOp",EDGE,"E136.trimOffspring");Q152=makeQuery(id+"F1.imprint","IMPRINT",FACE,{"disambiguationData":[TD([[makeQuery(id+"F1.imprint","IMPRINT",EDGE,{"derivedFrom":subQ0}),1.0]])]});}
            var Q153;
            {var subQ0=sQuery(id+"F1.wireOp",EDGE,"E84");var subQ1=sQuery(id+"F1.wireOp",EDGE,"E4");var subQ2=makeQuery(id+"F1.imprint","INTERSECT",VERTEX,{"derivedFrom":[subQ1,subQ0]});Q153=makeQuery(id+"F1.imprint","IMPRINT",FACE,{"disambiguationData":[TD([[makeQuery(id+"F1.imprint","IMPRINT",EDGE,{"disambiguationData":[TD([[subQ2,1.0]])],"derivedFrom":subQ1}),1.0]])]});}
            var Q154;
            {var subQ0=sQuery(id+"F1.wireOp",EDGE,"E84");var subQ1=sQuery(id+"F1.wireOp",EDGE,"E2");var subQ2=makeQuery(id+"F1.imprint","INTERSECT",VERTEX,{"derivedFrom":[subQ1,subQ0]});Q154=makeQuery(id+"F1.imprint","IMPRINT",FACE,{"disambiguationData":[TD([[makeQuery(id+"F1.imprint","IMPRINT",EDGE,{"disambiguationData":[TD([[subQ2,-1.0]])],"derivedFrom":subQ1}),1.0]])]});}
            var Q155;
            {var subQ0=sQuery(id+"F1.wireOp",EDGE,"E3");Q155=makeQuery(id+"F1.imprint","IMPRINT",FACE,{"disambiguationData":[TD([[makeQuery(id+"F1.imprint","IMPRINT",EDGE,{"derivedFrom":subQ0}),1.0]])]});}
            var Q156;
            {var subQ0=sQuery(id+"F1.wireOp",EDGE,"E86.trimOffspring");Q156=makeQuery(id+"F1.imprint","IMPRINT",FACE,{"disambiguationData":[TD([[makeQuery(id+"F1.imprint","IMPRINT",EDGE,{"derivedFrom":subQ0}),-1.0]])]});}
            var Q157;
            {var subQ0=sQuery(id+"F1.wireOp",EDGE,"E156.trimOffspring");Q157=makeQuery(id+"F1.imprint","IMPRINT",FACE,{"disambiguationData":[TD([[makeQuery(id+"F1.imprint","IMPRINT",EDGE,{"derivedFrom":subQ0}),1.0]])]});}
            var Q158;
            {var subQ0=sQuery(id+"F1.wireOp",EDGE,"E1");Q158=makeQuery(id+"F1.imprint","IMPRINT",FACE,{"disambiguationData":[TD([[makeQuery(id+"F1.imprint","IMPRINT",EDGE,{"derivedFrom":subQ0}),-1.0]])]});}
            extrude(context, id + "F2", {"entities" : qUnion([Q0, Q1, Q2, Q3, Q4, Q5, Q6, Q7, Q8, Q9, Q10, Q11, Q12, Q13, Q14, Q15, Q16, Q17, Q18, Q19, Q20, Q21, Q22, Q23, Q24, Q25, Q26, Q27, Q28, Q29, Q30, Q31, Q32, Q33, Q34, Q35, Q36, Q37, Q38, Q39, Q40, Q41, Q42, Q43, Q44, Q45, Q46, Q47, Q48, Q49, Q50, Q51, Q52, Q53, Q54, Q55, Q56, Q57, Q58, Q59, Q60, Q61, Q62, Q63, Q64, Q65, Q66, Q67, Q68, Q69, Q70, Q71, Q72, Q73, Q74, Q75, Q76, Q77, Q78, Q79, Q80, Q81, Q82, Q83, Q84, Q85, Q86, Q87, Q88, Q89, Q90, Q91, Q92, Q93, Q94, Q95, Q96, Q97, Q98, Q99, Q100, Q101, Q102, Q103, Q104, Q105, Q106, Q107, Q108, Q109, Q110, Q111, Q112, Q113, Q114, Q115, Q116, Q117, Q118, Q119, Q120, Q121, Q122, Q123, Q124, Q125, Q126, Q127, Q128, Q129, Q130, Q131, Q132, Q133, Q134, Q135, Q136, Q137, Q138, Q139, Q140, Q141, Q142, Q143, Q144, Q145, Q146, Q147, Q148, Q149, Q150, Q151, Q152, Q153, Q154, Q155, Q156, Q157, Q158]), "depth" : 3416 * mm, "offsetDistance" : 25 * mm});
        }
        {
            var Q0;
            Q0=makeQuery(id+"F2.opExtrude","SWEPT_FACE",FACE,{"disambiguationData":[OSD([sQuery(id+"F1.wireOp",EDGE,"E2")])]});
            var sketch = newSketch(context, id + "F3", { "sketchPlane" : qUnion([Q0])});
            skPoint(sketch, "E164", {"position": v(-4201, 3416) * mm});
            skLineSegment(sketch, "E165", {"start": v(-4201, 3416) * mm, "end": v(-4201, 3416) * mm});
            skLineSegment(sketch, "E166", {"start": v(-4201, 3916) * mm, "end": v(-4201, 3416) * mm});
            skLineSegment(sketch, "E167", {"start": v(-4201, 3416) * mm, "end": v(-3851, 3416) * mm});
            skLineSegment(sketch, "E168", {"start": v(-3851, 3416) * mm, "end": v(-3851, 3916) * mm});
            skLineSegment(sketch, "E169", {"start": v(-3851, 3916) * mm, "end": v(-4201, 3916) * mm});
            skSolve(sketch);
        }
        {
            var Q0;
            {var subQ0=sQuery(id+"F1.wireOp",EDGE,"E151.trimOffspring");var subQ1=sQuery(id+"F1.wireOp",EDGE,"E83.0");var subQ2=sQuery(id+"F1.wireOp",EDGE,"E85");var subQ4=sQuery(id+"F1.wireOp",EDGE,"E154");var subQ5=sQuery(id+"F1.wireOp",EDGE,"E82.0");var subQ7=sQuery(id+"F1.wireOp",EDGE,"E155.trimOffspring");var subQ8=sQuery(id+"F1.wireOp",EDGE,"E81.0");var subQ10=sQuery(id+"F1.wireOp",EDGE,"E150.trimOffspring");var subQ11=sQuery(id+"F1.wireOp",EDGE,"E80.0");var subQ13=sQuery(id+"F1.wireOp",EDGE,"E153");var subQ14=sQuery(id+"F1.wireOp",EDGE,"E79.0");var subQ16=sQuery(id+"F1.wireOp",EDGE,"E152");var subQ17=sQuery(id+"F1.wireOp",EDGE,"E78.0");var subQ19=sQuery(id+"F1.wireOp",EDGE,"E149.trimOffspring");var subQ20=sQuery(id+"F1.wireOp",EDGE,"E77.0");var subQ22=sQuery(id+"F1.wireOp",EDGE,"E148.trimOffspring");var subQ23=sQuery(id+"F1.wireOp",EDGE,"E76.0");var subQ25=sQuery(id+"F1.wireOp",EDGE,"E147.trimOffspring");var subQ26=sQuery(id+"F1.wireOp",EDGE,"E75.0");var subQ28=sQuery(id+"F1.wireOp",EDGE,"E145.trimOffspring");var subQ29=sQuery(id+"F1.wireOp",EDGE,"E74.0");var subQ31=sQuery(id+"F1.wireOp",EDGE,"E146.trimOffspring");var subQ32=sQuery(id+"F1.wireOp",EDGE,"E73.0");var subQ34=sQuery(id+"F1.wireOp",EDGE,"E144.trimOffspring");var subQ35=sQuery(id+"F1.wireOp",EDGE,"E72.0");var subQ37=sQuery(id+"F1.wireOp",EDGE,"E163");var subQ38=sQuery(id+"F1.wireOp",EDGE,"E71.0");var subQ40=sQuery(id+"F1.wireOp",EDGE,"E143.trimOffspring");var subQ41=sQuery(id+"F1.wireOp",EDGE,"E70.0");var subQ43=sQuery(id+"F1.wireOp",EDGE,"E142.trimOffspring");var subQ44=sQuery(id+"F1.wireOp",EDGE,"E69.0");var subQ46=sQuery(id+"F1.wireOp",EDGE,"E139.trimOffspring");var subQ47=sQuery(id+"F1.wireOp",EDGE,"E68.0");var subQ49=sQuery(id+"F1.wireOp",EDGE,"E140.trimOffspring");var subQ50=sQuery(id+"F1.wireOp",EDGE,"E67.0");var subQ52=sQuery(id+"F1.wireOp",EDGE,"E138.trimOffspring");var subQ53=sQuery(id+"F1.wireOp",EDGE,"E66.0");var subQ55=sQuery(id+"F1.wireOp",EDGE,"E141");var subQ56=sQuery(id+"F1.wireOp",EDGE,"E65.0");var subQ58=sQuery(id+"F1.wireOp",EDGE,"E134.trimOffspring");var subQ59=sQuery(id+"F1.wireOp",EDGE,"E64.0");var subQ61=sQuery(id+"F1.wireOp",EDGE,"E137");var subQ62=sQuery(id+"F1.wireOp",EDGE,"E63.0");var subQ64=sQuery(id+"F1.wireOp",EDGE,"E135.trimOffspring");var subQ65=sQuery(id+"F1.wireOp",EDGE,"E62.0");var subQ67=sQuery(id+"F1.wireOp",EDGE,"E19.0");var subQ69=sQuery(id+"F1.wireOp",EDGE,"E58.0");var subQ71=sQuery(id+"F1.wireOp",EDGE,"E159");var subQ72=sQuery(id+"F1.wireOp",EDGE,"E9.0");var subQ74=sQuery(id+"F1.wireOp",EDGE,"E136.trimOffspring");var subQ75=sQuery(id+"F1.wireOp",EDGE,"E61.0");var subQ77=sQuery(id+"F1.wireOp",EDGE,"E162");var subQ78=sQuery(id+"F1.wireOp",EDGE,"E17.0");var subQ80=sQuery(id+"F1.wireOp",EDGE,"E56.0");var subQ82=sQuery(id+"F1.wireOp",EDGE,"E158.trimOffspring");var subQ83=sQuery(id+"F1.wireOp",EDGE,"E8.0");var subQ85=sQuery(id+"F1.wireOp",EDGE,"E133.trimOffspring");var subQ86=sQuery(id+"F1.wireOp",EDGE,"E60.0");var subQ88=sQuery(id+"F1.wireOp",EDGE,"E160");var subQ89=sQuery(id+"F1.wireOp",EDGE,"E15.0");var subQ91=sQuery(id+"F1.wireOp",EDGE,"E54.0");var subQ93=sQuery(id+"F1.wireOp",EDGE,"E125.trimOffspring");var subQ94=sQuery(id+"F1.wireOp",EDGE,"E7.0");var subQ96=sQuery(id+"F1.wireOp",EDGE,"E161");var subQ97=sQuery(id+"F1.wireOp",EDGE,"E59.0");var subQ99=sQuery(id+"F1.wireOp",EDGE,"E13.0");var subQ101=sQuery(id+"F1.wireOp",EDGE,"E52.0");var subQ103=sQuery(id+"F1.wireOp",EDGE,"E6.0");var subQ105=sQuery(id+"F1.wireOp",EDGE,"E129.trimOffspring");var subQ106=sQuery(id+"F1.wireOp",EDGE,"E156.trimOffspring");var subQ107=sQuery(id+"F1.wireOp",EDGE,"E11.0");var subQ109=sQuery(id+"F1.wireOp",EDGE,"E50.0");var subQ111=sQuery(id+"F1.wireOp",EDGE,"E5.0");var subQ112=sQuery(id+"F1.wireOp",EDGE,"E3");var subQ114=sQuery(id+"F1.wireOp",EDGE,"E132");var subQ115=sQuery(id+"F1.wireOp",EDGE,"E57.0");var subQ117=sQuery(id+"F1.wireOp",EDGE,"E48.0");var subQ119=sQuery(id+"F1.wireOp",EDGE,"E4");var subQ120=sQuery(id+"F1.wireOp",EDGE,"E130.trimOffspring");var subQ121=sQuery(id+"F1.wireOp",EDGE,"E46.0");var subQ123=sQuery(id+"F1.wireOp",EDGE,"E2");var subQ124=sQuery(id+"F1.wireOp",EDGE,"E128.trimOffspring");var subQ125=sQuery(id+"F1.wireOp",EDGE,"E55.0");var subQ127=sQuery(id+"F1.wireOp",EDGE,"E131");var subQ128=sQuery(id+"F1.wireOp",EDGE,"E157.trimOffspring");var subQ129=sQuery(id+"F1.wireOp",EDGE,"E51.0");var subQ131=sQuery(id+"F1.wireOp",EDGE,"E126.trimOffspring");var subQ132=sQuery(id+"F1.wireOp",EDGE,"E49.0");var subQ134=sQuery(id+"F1.wireOp",EDGE,"E24.0");var subQ136=sQuery(id+"F1.wireOp",EDGE,"E23.0");var subQ138=sQuery(id+"F1.wireOp",EDGE,"E22.0");var subQ140=sQuery(id+"F1.wireOp",EDGE,"E44.0");var subQ142=sQuery(id+"F1.wireOp",EDGE,"E20.0");var subQ144=sQuery(id+"F1.wireOp",EDGE,"E42.0");var subQ146=sQuery(id+"F1.wireOp",EDGE,"E40.0");var subQ148=sQuery(id+"F1.wireOp",EDGE,"E18.0");var subQ150=sQuery(id+"F1.wireOp",EDGE,"E38.0");var subQ152=sQuery(id+"F1.wireOp",EDGE,"E36.0");var subQ154=sQuery(id+"F1.wireOp",EDGE,"E16.0");var subQ156=sQuery(id+"F1.wireOp",EDGE,"E34.0");var subQ158=sQuery(id+"F1.wireOp",EDGE,"E14.0");var subQ160=sQuery(id+"F1.wireOp",EDGE,"E30.0");var subQ162=sQuery(id+"F1.wireOp",EDGE,"E127.trimOffspring");var subQ163=sQuery(id+"F1.wireOp",EDGE,"E28.0");var subQ165=sQuery(id+"F1.wireOp",EDGE,"E12.0");var subQ167=sQuery(id+"F1.wireOp",EDGE,"E26.0");var subQ169=sQuery(id+"F1.wireOp",EDGE,"E32.0");var subQ171=sQuery(id+"F1.wireOp",EDGE,"E53.0");var subQ173=sQuery(id+"F1.wireOp",EDGE,"E47.0");var subQ175=sQuery(id+"F1.wireOp",EDGE,"E10.0");var subQ177=sQuery(id+"F1.wireOp",EDGE,"E25.0");var subQ179=sQuery(id+"F1.wireOp",EDGE,"E27.0");var subQ181=sQuery(id+"F1.wireOp",EDGE,"E29.0");var subQ183=sQuery(id+"F1.wireOp",EDGE,"E31.0");var subQ185=sQuery(id+"F1.wireOp",EDGE,"E33.0");var subQ187=sQuery(id+"F1.wireOp",EDGE,"E35.0");var subQ189=sQuery(id+"F1.wireOp",EDGE,"E37.0");var subQ191=sQuery(id+"F1.wireOp",EDGE,"E39.0");var subQ193=sQuery(id+"F1.wireOp",EDGE,"E41.0");var subQ195=sQuery(id+"F1.wireOp",EDGE,"E43.0");var subQ197=sQuery(id+"F1.wireOp",EDGE,"E45.0");Q0=makeQuery(id+"FzMqNVo3a2xKz4z_1.boolean.opBoolean","SPLIT",FACE,{"disambiguationData":[TD([makeQuery(id+"F2.opExtrude","SWEPT_FACE",FACE,{"disambiguationData":[OSD([subQ112])]})])],"derivedFrom":makeQuery(id+"F2.opExtrude","CAP_FACE",FACE,{"disambiguationData":[OSD([sQuery(id+"F1.wireOp",EDGE,"E1"),subQ123,subQ112,subQ119,subQ111,subQ103,subQ94,subQ83,subQ72,subQ175,subQ107,subQ165,subQ99,subQ158,subQ89,subQ154,subQ78,subQ148,subQ67,subQ142,subQ138,subQ136,subQ134,subQ177,subQ167,subQ179,subQ163,subQ181,subQ160,subQ183,subQ169,subQ185,subQ156,subQ187,subQ152,subQ189,subQ150,subQ191,subQ146,subQ193,subQ144,subQ195,subQ140,subQ197,subQ121,subQ173,subQ117,subQ132,subQ109,subQ129,subQ101,subQ171,subQ91,subQ125,subQ80,subQ115,subQ69,subQ97,subQ86,subQ75,subQ65,subQ62,subQ59,subQ56,subQ53,subQ50,subQ47,subQ44,subQ41,subQ38,subQ35,subQ32,subQ29,subQ26,subQ23,subQ20,subQ17,subQ14,subQ11,subQ8,subQ5,subQ1,sQuery(id+"F1.wireOp",EDGE,"E84"),subQ2,sQuery(id+"F1.wireOp",EDGE,"E86.trimOffspring"),sQuery(id+"F1.wireOp",EDGE,"E87.trimOffspring"),sQuery(id+"F1.wireOp",EDGE,"E88.trimOffspring"),sQuery(id+"F1.wireOp",EDGE,"E89.trimOffspring"),sQuery(id+"F1.wireOp",EDGE,"E90.trimOffspring"),sQuery(id+"F1.wireOp",EDGE,"E91.trimOffspring"),sQuery(id+"F1.wireOp",EDGE,"E92.trimOffspring"),sQuery(id+"F1.wireOp",EDGE,"E93.trimOffspring"),sQuery(id+"F1.wireOp",EDGE,"E94.trimOffspring"),sQuery(id+"F1.wireOp",EDGE,"E95.trimOffspring"),sQuery(id+"F1.wireOp",EDGE,"E96.trimOffspring"),sQuery(id+"F1.wireOp",EDGE,"E97.trimOffspring"),sQuery(id+"F1.wireOp",EDGE,"E98.trimOffspring"),sQuery(id+"F1.wireOp",EDGE,"E99.trimOffspring"),sQuery(id+"F1.wireOp",EDGE,"E100.trimOffspring"),sQuery(id+"F1.wireOp",EDGE,"E101.trimOffspring"),sQuery(id+"F1.wireOp",EDGE,"E102.trimOffspring"),sQuery(id+"F1.wireOp",EDGE,"E103.trimOffspring"),sQuery(id+"F1.wireOp",EDGE,"E104.trimOffspring"),sQuery(id+"F1.wireOp",EDGE,"E105.trimOffspring"),sQuery(id+"F1.wireOp",EDGE,"E106.trimOffspring"),sQuery(id+"F1.wireOp",EDGE,"E107.trimOffspring"),sQuery(id+"F1.wireOp",EDGE,"E108.trimOffspring"),sQuery(id+"F1.wireOp",EDGE,"E109.trimOffspring"),sQuery(id+"F1.wireOp",EDGE,"E110.trimOffspring"),sQuery(id+"F1.wireOp",EDGE,"E111.trimOffspring"),sQuery(id+"F1.wireOp",EDGE,"E112.trimOffspring"),sQuery(id+"F1.wireOp",EDGE,"E113.trimOffspring"),sQuery(id+"F1.wireOp",EDGE,"E114.trimOffspring"),sQuery(id+"F1.wireOp",EDGE,"E115.trimOffspring"),sQuery(id+"F1.wireOp",EDGE,"E116.trimOffspring"),sQuery(id+"F1.wireOp",EDGE,"E117.trimOffspring"),sQuery(id+"F1.wireOp",EDGE,"E118.trimOffspring"),sQuery(id+"F1.wireOp",EDGE,"E119.trimOffspring"),sQuery(id+"F1.wireOp",EDGE,"E120.trimOffspring"),sQuery(id+"F1.wireOp",EDGE,"E121.trimOffspring"),sQuery(id+"F1.wireOp",EDGE,"E122.trimOffspring"),sQuery(id+"F1.wireOp",EDGE,"E123.trimOffspring"),sQuery(id+"F1.wireOp",EDGE,"E124.trimOffspring"),subQ93,subQ131,subQ162,subQ124,subQ105,subQ120,subQ127,subQ114,subQ85,subQ58,subQ64,subQ74,subQ61,subQ52,subQ46,subQ49,subQ55,subQ43,subQ40,subQ34,subQ28,subQ31,subQ25,subQ22,subQ19,subQ10,subQ0,subQ16,subQ13,subQ4,subQ7,subQ106,subQ128,subQ82,subQ71,subQ88,subQ96,subQ77,subQ37])],"isStart":false})});}
            var sketch = newSketch(context, id + "F4", { "sketchPlane" : qUnion([Q0])});
            skLineSegment(sketch, "E170", {"start": v(-17701.46, 3643) * mm, "end": v(-15201.46, 3643) * mm});
            skLineSegment(sketch, "E171", {"start": v(-15201.46, 3643) * mm, "end": v(-15201.46, 3293) * mm});
            skLineSegment(sketch, "E172", {"start": v(-15201.46, 3293) * mm, "end": v(-17701.46, 3293) * mm});
            skLineSegment(sketch, "E173", {"start": v(-17701.46, 3293) * mm, "end": v(-17701.46, 3643) * mm});
            skPoint(sketch, "E174.startSnap0", {"position": v(-17426.46, 2618) * mm});
            skLineSegment(sketch, "E175", {"start": v(-20201.46, 2493) * mm, "end": v(-20929.97, 2493) * mm});
            skLineSegment(sketch, "E176", {"start": v(-20929.97, 2493) * mm, "end": v(-20929.97, 3878) * mm});
            skSolve(sketch);
        }
        {
            var Q0;
            {var subQ0=sQuery(id+"F1.wireOp",EDGE,"E151.trimOffspring");var subQ1=sQuery(id+"F1.wireOp",EDGE,"E83.0");var subQ2=sQuery(id+"F1.wireOp",EDGE,"E85");var subQ4=sQuery(id+"F1.wireOp",EDGE,"E154");var subQ5=sQuery(id+"F1.wireOp",EDGE,"E82.0");var subQ7=sQuery(id+"F1.wireOp",EDGE,"E155.trimOffspring");var subQ8=sQuery(id+"F1.wireOp",EDGE,"E81.0");var subQ10=sQuery(id+"F1.wireOp",EDGE,"E150.trimOffspring");var subQ11=sQuery(id+"F1.wireOp",EDGE,"E80.0");var subQ13=sQuery(id+"F1.wireOp",EDGE,"E153");var subQ14=sQuery(id+"F1.wireOp",EDGE,"E79.0");var subQ16=sQuery(id+"F1.wireOp",EDGE,"E152");var subQ17=sQuery(id+"F1.wireOp",EDGE,"E78.0");var subQ19=sQuery(id+"F1.wireOp",EDGE,"E149.trimOffspring");var subQ20=sQuery(id+"F1.wireOp",EDGE,"E77.0");var subQ22=sQuery(id+"F1.wireOp",EDGE,"E148.trimOffspring");var subQ23=sQuery(id+"F1.wireOp",EDGE,"E76.0");var subQ25=sQuery(id+"F1.wireOp",EDGE,"E147.trimOffspring");var subQ26=sQuery(id+"F1.wireOp",EDGE,"E75.0");var subQ28=sQuery(id+"F1.wireOp",EDGE,"E145.trimOffspring");var subQ29=sQuery(id+"F1.wireOp",EDGE,"E74.0");var subQ31=sQuery(id+"F1.wireOp",EDGE,"E146.trimOffspring");var subQ32=sQuery(id+"F1.wireOp",EDGE,"E73.0");var subQ34=sQuery(id+"F1.wireOp",EDGE,"E144.trimOffspring");var subQ35=sQuery(id+"F1.wireOp",EDGE,"E72.0");var subQ37=sQuery(id+"F1.wireOp",EDGE,"E163");var subQ38=sQuery(id+"F1.wireOp",EDGE,"E71.0");var subQ40=sQuery(id+"F1.wireOp",EDGE,"E143.trimOffspring");var subQ41=sQuery(id+"F1.wireOp",EDGE,"E70.0");var subQ43=sQuery(id+"F1.wireOp",EDGE,"E142.trimOffspring");var subQ44=sQuery(id+"F1.wireOp",EDGE,"E69.0");var subQ46=sQuery(id+"F1.wireOp",EDGE,"E139.trimOffspring");var subQ47=sQuery(id+"F1.wireOp",EDGE,"E68.0");var subQ49=sQuery(id+"F1.wireOp",EDGE,"E140.trimOffspring");var subQ50=sQuery(id+"F1.wireOp",EDGE,"E67.0");var subQ52=sQuery(id+"F1.wireOp",EDGE,"E138.trimOffspring");var subQ53=sQuery(id+"F1.wireOp",EDGE,"E66.0");var subQ55=sQuery(id+"F1.wireOp",EDGE,"E141");var subQ56=sQuery(id+"F1.wireOp",EDGE,"E65.0");var subQ58=sQuery(id+"F1.wireOp",EDGE,"E134.trimOffspring");var subQ59=sQuery(id+"F1.wireOp",EDGE,"E64.0");var subQ61=sQuery(id+"F1.wireOp",EDGE,"E137");var subQ62=sQuery(id+"F1.wireOp",EDGE,"E63.0");var subQ64=sQuery(id+"F1.wireOp",EDGE,"E135.trimOffspring");var subQ65=sQuery(id+"F1.wireOp",EDGE,"E62.0");var subQ67=sQuery(id+"F1.wireOp",EDGE,"E19.0");var subQ69=sQuery(id+"F1.wireOp",EDGE,"E58.0");var subQ71=sQuery(id+"F1.wireOp",EDGE,"E159");var subQ72=sQuery(id+"F1.wireOp",EDGE,"E9.0");var subQ74=sQuery(id+"F1.wireOp",EDGE,"E136.trimOffspring");var subQ75=sQuery(id+"F1.wireOp",EDGE,"E61.0");var subQ77=sQuery(id+"F1.wireOp",EDGE,"E162");var subQ78=sQuery(id+"F1.wireOp",EDGE,"E17.0");var subQ80=sQuery(id+"F1.wireOp",EDGE,"E56.0");var subQ82=sQuery(id+"F1.wireOp",EDGE,"E158.trimOffspring");var subQ83=sQuery(id+"F1.wireOp",EDGE,"E8.0");var subQ85=sQuery(id+"F1.wireOp",EDGE,"E133.trimOffspring");var subQ86=sQuery(id+"F1.wireOp",EDGE,"E60.0");var subQ88=sQuery(id+"F1.wireOp",EDGE,"E160");var subQ89=sQuery(id+"F1.wireOp",EDGE,"E15.0");var subQ91=sQuery(id+"F1.wireOp",EDGE,"E54.0");var subQ93=sQuery(id+"F1.wireOp",EDGE,"E125.trimOffspring");var subQ94=sQuery(id+"F1.wireOp",EDGE,"E7.0");var subQ96=sQuery(id+"F1.wireOp",EDGE,"E161");var subQ97=sQuery(id+"F1.wireOp",EDGE,"E59.0");var subQ99=sQuery(id+"F1.wireOp",EDGE,"E13.0");var subQ101=sQuery(id+"F1.wireOp",EDGE,"E52.0");var subQ103=sQuery(id+"F1.wireOp",EDGE,"E6.0");var subQ105=sQuery(id+"F1.wireOp",EDGE,"E129.trimOffspring");var subQ106=sQuery(id+"F1.wireOp",EDGE,"E156.trimOffspring");var subQ107=sQuery(id+"F1.wireOp",EDGE,"E11.0");var subQ109=sQuery(id+"F1.wireOp",EDGE,"E50.0");var subQ111=sQuery(id+"F1.wireOp",EDGE,"E5.0");var subQ112=sQuery(id+"F1.wireOp",EDGE,"E3");var subQ114=sQuery(id+"F1.wireOp",EDGE,"E132");var subQ115=sQuery(id+"F1.wireOp",EDGE,"E57.0");var subQ117=sQuery(id+"F1.wireOp",EDGE,"E48.0");var subQ119=sQuery(id+"F1.wireOp",EDGE,"E4");var subQ120=sQuery(id+"F1.wireOp",EDGE,"E130.trimOffspring");var subQ121=sQuery(id+"F1.wireOp",EDGE,"E46.0");var subQ123=sQuery(id+"F1.wireOp",EDGE,"E2");var subQ124=sQuery(id+"F1.wireOp",EDGE,"E128.trimOffspring");var subQ125=sQuery(id+"F1.wireOp",EDGE,"E55.0");var subQ127=sQuery(id+"F1.wireOp",EDGE,"E131");var subQ128=sQuery(id+"F1.wireOp",EDGE,"E157.trimOffspring");var subQ129=sQuery(id+"F1.wireOp",EDGE,"E51.0");var subQ131=sQuery(id+"F1.wireOp",EDGE,"E126.trimOffspring");var subQ132=sQuery(id+"F1.wireOp",EDGE,"E49.0");var subQ134=sQuery(id+"F1.wireOp",EDGE,"E24.0");var subQ136=sQuery(id+"F1.wireOp",EDGE,"E23.0");var subQ138=sQuery(id+"F1.wireOp",EDGE,"E22.0");var subQ140=sQuery(id+"F1.wireOp",EDGE,"E44.0");var subQ142=sQuery(id+"F1.wireOp",EDGE,"E20.0");var subQ144=sQuery(id+"F1.wireOp",EDGE,"E42.0");var subQ146=sQuery(id+"F1.wireOp",EDGE,"E40.0");var subQ148=sQuery(id+"F1.wireOp",EDGE,"E18.0");var subQ150=sQuery(id+"F1.wireOp",EDGE,"E38.0");var subQ152=sQuery(id+"F1.wireOp",EDGE,"E36.0");var subQ154=sQuery(id+"F1.wireOp",EDGE,"E16.0");var subQ156=sQuery(id+"F1.wireOp",EDGE,"E34.0");var subQ158=sQuery(id+"F1.wireOp",EDGE,"E14.0");var subQ160=sQuery(id+"F1.wireOp",EDGE,"E30.0");var subQ162=sQuery(id+"F1.wireOp",EDGE,"E127.trimOffspring");var subQ163=sQuery(id+"F1.wireOp",EDGE,"E28.0");var subQ165=sQuery(id+"F1.wireOp",EDGE,"E12.0");var subQ167=sQuery(id+"F1.wireOp",EDGE,"E26.0");var subQ169=sQuery(id+"F1.wireOp",EDGE,"E32.0");var subQ171=sQuery(id+"F1.wireOp",EDGE,"E53.0");var subQ173=sQuery(id+"F1.wireOp",EDGE,"E47.0");var subQ175=sQuery(id+"F1.wireOp",EDGE,"E10.0");var subQ177=sQuery(id+"F1.wireOp",EDGE,"E25.0");var subQ179=sQuery(id+"F1.wireOp",EDGE,"E27.0");var subQ181=sQuery(id+"F1.wireOp",EDGE,"E29.0");var subQ183=sQuery(id+"F1.wireOp",EDGE,"E31.0");var subQ185=sQuery(id+"F1.wireOp",EDGE,"E33.0");var subQ187=sQuery(id+"F1.wireOp",EDGE,"E35.0");var subQ189=sQuery(id+"F1.wireOp",EDGE,"E37.0");var subQ191=sQuery(id+"F1.wireOp",EDGE,"E39.0");var subQ193=sQuery(id+"F1.wireOp",EDGE,"E41.0");var subQ195=sQuery(id+"F1.wireOp",EDGE,"E43.0");var subQ197=sQuery(id+"F1.wireOp",EDGE,"E45.0");Q0=makeQuery(id+"FzMqNVo3a2xKz4z_1.boolean.opBoolean","SPLIT",FACE,{"disambiguationData":[TD([makeQuery(id+"F2.opExtrude","SWEPT_FACE",FACE,{"disambiguationData":[OSD([subQ112])]})])],"derivedFrom":makeQuery(id+"F2.opExtrude","CAP_FACE",FACE,{"disambiguationData":[OSD([sQuery(id+"F1.wireOp",EDGE,"E1"),subQ123,subQ112,subQ119,subQ111,subQ103,subQ94,subQ83,subQ72,subQ175,subQ107,subQ165,subQ99,subQ158,subQ89,subQ154,subQ78,subQ148,subQ67,subQ142,subQ138,subQ136,subQ134,subQ177,subQ167,subQ179,subQ163,subQ181,subQ160,subQ183,subQ169,subQ185,subQ156,subQ187,subQ152,subQ189,subQ150,subQ191,subQ146,subQ193,subQ144,subQ195,subQ140,subQ197,subQ121,subQ173,subQ117,subQ132,subQ109,subQ129,subQ101,subQ171,subQ91,subQ125,subQ80,subQ115,subQ69,subQ97,subQ86,subQ75,subQ65,subQ62,subQ59,subQ56,subQ53,subQ50,subQ47,subQ44,subQ41,subQ38,subQ35,subQ32,subQ29,subQ26,subQ23,subQ20,subQ17,subQ14,subQ11,subQ8,subQ5,subQ1,sQuery(id+"F1.wireOp",EDGE,"E84"),subQ2,sQuery(id+"F1.wireOp",EDGE,"E86.trimOffspring"),sQuery(id+"F1.wireOp",EDGE,"E87.trimOffspring"),sQuery(id+"F1.wireOp",EDGE,"E88.trimOffspring"),sQuery(id+"F1.wireOp",EDGE,"E89.trimOffspring"),sQuery(id+"F1.wireOp",EDGE,"E90.trimOffspring"),sQuery(id+"F1.wireOp",EDGE,"E91.trimOffspring"),sQuery(id+"F1.wireOp",EDGE,"E92.trimOffspring"),sQuery(id+"F1.wireOp",EDGE,"E93.trimOffspring"),sQuery(id+"F1.wireOp",EDGE,"E94.trimOffspring"),sQuery(id+"F1.wireOp",EDGE,"E95.trimOffspring"),sQuery(id+"F1.wireOp",EDGE,"E96.trimOffspring"),sQuery(id+"F1.wireOp",EDGE,"E97.trimOffspring"),sQuery(id+"F1.wireOp",EDGE,"E98.trimOffspring"),sQuery(id+"F1.wireOp",EDGE,"E99.trimOffspring"),sQuery(id+"F1.wireOp",EDGE,"E100.trimOffspring"),sQuery(id+"F1.wireOp",EDGE,"E101.trimOffspring"),sQuery(id+"F1.wireOp",EDGE,"E102.trimOffspring"),sQuery(id+"F1.wireOp",EDGE,"E103.trimOffspring"),sQuery(id+"F1.wireOp",EDGE,"E104.trimOffspring"),sQuery(id+"F1.wireOp",EDGE,"E105.trimOffspring"),sQuery(id+"F1.wireOp",EDGE,"E106.trimOffspring"),sQuery(id+"F1.wireOp",EDGE,"E107.trimOffspring"),sQuery(id+"F1.wireOp",EDGE,"E108.trimOffspring"),sQuery(id+"F1.wireOp",EDGE,"E109.trimOffspring"),sQuery(id+"F1.wireOp",EDGE,"E110.trimOffspring"),sQuery(id+"F1.wireOp",EDGE,"E111.trimOffspring"),sQuery(id+"F1.wireOp",EDGE,"E112.trimOffspring"),sQuery(id+"F1.wireOp",EDGE,"E113.trimOffspring"),sQuery(id+"F1.wireOp",EDGE,"E114.trimOffspring"),sQuery(id+"F1.wireOp",EDGE,"E115.trimOffspring"),sQuery(id+"F1.wireOp",EDGE,"E116.trimOffspring"),sQuery(id+"F1.wireOp",EDGE,"E117.trimOffspring"),sQuery(id+"F1.wireOp",EDGE,"E118.trimOffspring"),sQuery(id+"F1.wireOp",EDGE,"E119.trimOffspring"),sQuery(id+"F1.wireOp",EDGE,"E120.trimOffspring"),sQuery(id+"F1.wireOp",EDGE,"E121.trimOffspring"),sQuery(id+"F1.wireOp",EDGE,"E122.trimOffspring"),sQuery(id+"F1.wireOp",EDGE,"E123.trimOffspring"),sQuery(id+"F1.wireOp",EDGE,"E124.trimOffspring"),subQ93,subQ131,subQ162,subQ124,subQ105,subQ120,subQ127,subQ114,subQ85,subQ58,subQ64,subQ74,subQ61,subQ52,subQ46,subQ49,subQ55,subQ43,subQ40,subQ34,subQ28,subQ31,subQ25,subQ22,subQ19,subQ10,subQ0,subQ16,subQ13,subQ4,subQ7,subQ106,subQ128,subQ82,subQ71,subQ88,subQ96,subQ77,subQ37])],"isStart":false})});}
            var sketch = newSketch(context, id + "F5", { "sketchPlane" : qUnion([Q0])});
            skLineSegment(sketch, "E177", {"start": v(-17701.46, 3201) * mm, "end": v(-17701.46, 2851) * mm});
            skLineSegment(sketch, "E178", {"start": v(-17701.46, 2851) * mm, "end": v(-16785.46, 2851) * mm});
            skLineSegment(sketch, "E179", {"start": v(-16785.46, 2851) * mm, "end": v(-16785.46, 3201) * mm});
            skLineSegment(sketch, "E180", {"start": v(-16785.46, 3201) * mm, "end": v(-17701.46, 3201) * mm});
            skLineSegment(sketch, "E181.MirrorCS", {"start": v(-16117.46, 2851) * mm, "end": v(-16117.46, 3201) * mm});
            skLineSegment(sketch, "E182.MirrorCS", {"start": v(-16117.46, 3201) * mm, "end": v(-15201.46, 3201) * mm});
            skLineSegment(sketch, "E183.MirrorCS", {"start": v(-15201.46, 2851) * mm, "end": v(-16117.46, 2851) * mm});
            skLineSegment(sketch, "E184.MirrorCS", {"start": v(-15201.46, 3201) * mm, "end": v(-15201.46, 2851) * mm});
            skSolve(sketch);
        }
        {
            var Q0;
            Q0=makeQuery(id+"F5.imprint","IMPRINT",FACE,{"disambiguationData":[TD([[makeQuery(id+"F5.imprint","IMPRINT",EDGE,{"derivedFrom":sQuery(id+"F5.wireOp",EDGE,"E177")}),1.0]])]});
            var Q1;
            Q1=makeQuery(id+"F5.imprint","IMPRINT",FACE,{"disambiguationData":[TD([[makeQuery(id+"F5.imprint","IMPRINT",EDGE,{"derivedFrom":sQuery(id+"F5.wireOp",EDGE,"E181.MirrorCS")}),-1.0]])]});
            extrude(context, id + "F6", {"entities" : qUnion([Q0, Q1]), "operationType" : NewBodyOperationType.ADD, "depth" : 1044 * mm, "offsetDistance" : 25 * mm});
        }
        {
            var Q0;
            Q0=makeQuery(id+"F4.imprint","IMPRINT",FACE,{"disambiguationData":[TD([[makeQuery(id+"F4.imprint","IMPRINT",EDGE,{"derivedFrom":sQuery(id+"F4.wireOp",EDGE,"E170")}),-1.0]])]});
            extrude(context, id + "F7", {"entities" : qUnion([Q0]), "operationType" : NewBodyOperationType.ADD, "depth" : 800 * mm, "offsetDistance" : 25 * mm});
        }
        {
            var Q0;
            Q0=makeQuery(id+"F7RHQ93fltytKVB_1.boolean.opBoolean","MERGE",FACE,{"derivedFrom":[makeQuery(id+"F2.opExtrude","SWEPT_FACE",FACE,{"disambiguationData":[OSD([sQuery(id+"F1.wireOp",EDGE,"E2")])]}),makeQuery(id+"F7RHQ93fltytKVB_1.opExtrude","CAP_FACE",FACE,{"disambiguationData":[OSD([sQuery(id+"F3.wireOp",EDGE,"E166"),sQuery(id+"F3.wireOp",EDGE,"E167"),sQuery(id+"F3.wireOp",EDGE,"E168"),sQuery(id+"F3.wireOp",EDGE,"E169")])],"isStart":true})]});
            var sketch = newSketch(context, id + "F8", { "sketchPlane" : qUnion([Q0])});
            skLineSegment(sketch, "E185", {"start": v(-4551, 3416) * mm, "end": v(-4551, 3916) * mm});
            skLineSegment(sketch, "E186", {"start": v(-4551, 3916) * mm, "end": v(-4901, 3916) * mm});
            skLineSegment(sketch, "E187", {"start": v(-4901, 3916) * mm, "end": v(-4901, 3416) * mm});
            skLineSegment(sketch, "E188", {"start": v(-4901, 3416) * mm, "end": v(-4551, 3416) * mm});
            skSolve(sketch);
        }
        {
            var Q0;
            Q0=makeQuery(id+"F8.imprint","IMPRINT",FACE,{"disambiguationData":[TD([[makeQuery(id+"F8.imprint","IMPRINT",EDGE,{"derivedFrom":sQuery(id+"F8.wireOp",EDGE,"E185")}),1.0]])]});
            extrude(context, id + "F9", {"entities" : qUnion([Q0]), "operationType" : NewBodyOperationType.ADD, "oppositeDirection" : true, "depth" : 11725 * mm, "offsetDistance" : 25 * mm});
        }
        {
            var Q0;
            Q0=makeQuery(id+"F6.opExtrude","SWEPT_FACE",FACE,{"disambiguationData":[OSD([sQuery(id+"F5.wireOp",EDGE,"E184.MirrorCS")])]});
            var sketch = newSketch(context, id + "F10", { "sketchPlane" : qUnion([Q0])});
            skLineSegment(sketch, "E189", {"start": v(2851, 4460) * mm, "end": v(3201, 4460) * mm});
            skLineSegment(sketch, "E190", {"start": v(3201, 4460) * mm, "end": v(3201, 3960) * mm});
            skLineSegment(sketch, "E191", {"start": v(3201, 3960) * mm, "end": v(2851, 3960) * mm});
            skLineSegment(sketch, "E192", {"start": v(2851, 3960) * mm, "end": v(2851, 4460) * mm});
            skSolve(sketch);
        }
        {
            var Q0;
            Q0=makeQuery(id+"F10.imprint","IMPRINT",FACE,{"disambiguationData":[TD([[makeQuery(id+"F10.imprint","IMPRINT",EDGE,{"derivedFrom":sQuery(id+"F10.wireOp",EDGE,"E189")}),1.0]])]});
            extrude(context, id + "F11", {"entities" : qUnion([Q0]), "operationType" : NewBodyOperationType.ADD, "depth" : 500 * mm, "offsetDistance" : 25 * mm});
        }
        {
            var Q0;
            Q0=makeQuery(id+"F11.boolean.opBoolean","MERGE",FACE,{"derivedFrom":[makeQuery(id+"F6.opExtrude","CAP_FACE",FACE,{"disambiguationData":[OSD([sQuery(id+"F5.wireOp",EDGE,"E181.MirrorCS"),sQuery(id+"F5.wireOp",EDGE,"E182.MirrorCS"),sQuery(id+"F5.wireOp",EDGE,"E183.MirrorCS"),sQuery(id+"F5.wireOp",EDGE,"E184.MirrorCS")])],"isStart":false}),makeQuery(id+"F11.opExtrude","SWEPT_FACE",FACE,{"disambiguationData":[OSD([sQuery(id+"F10.wireOp",EDGE,"E189")])]})]});
            var sketch = newSketch(context, id + "F12", { "sketchPlane" : qUnion([Q0])});
            skLineSegment(sketch, "E193", {"start": v(-14701.46, 3201) * mm, "end": v(-14151.46, 3201) * mm});
            skLineSegment(sketch, "E194", {"start": v(-13976.46, 3376) * mm, "end": v(-13976.46, 4326) * mm});
            skLineSegment(sketch, "E195", {"start": v(-14701.46, 3201) * mm, "end": v(-14701.46, 2851) * mm});
            skLineSegment(sketch, "E196", {"start": v(-14701.46, 2851) * mm, "end": v(-14151.46, 2851) * mm});
            skPoint(sketch, "E197.visualSharp", {"position": v(-13626.46, 2851) * mm});
            skArc(sketch, "E197.filletArc", {"start": v(-14151.46, 2851) * mm, "mid": v(-13780.23, 3004.77) * mm, "end": v(-13626.46, 3376) * mm});
            skPoint(sketch, "E198.visualSharp", {"position": v(-13976.46, 3201) * mm});
            skArc(sketch, "E198.filletArc", {"start": v(-14151.46, 3201) * mm, "mid": v(-14027.72, 3252.26) * mm, "end": v(-13976.46, 3376) * mm});
            skLineSegment(sketch, "E199", {"start": v(-14051.46, 4551) * mm, "end": v(-13551.46, 4551) * mm});
            skLineSegment(sketch, "E200", {"start": v(-13626.46, 4326) * mm, "end": v(-13551.46, 4551) * mm});
            skLineSegment(sketch, "E201", {"start": v(-13976.46, 4326) * mm, "end": v(-14051.46, 4551) * mm});
            skLineSegment(sketch, "E202", {"start": v(-13626.46, 3376) * mm, "end": v(-13626.46, 4326) * mm});
            skLineSegment(sketch, "E203", {"start": v(-16201.46, 4135.96) * mm, "end": v(-16201.46, 1909.35) * mm});
            skLineSegment(sketch, "E204.MirrorCS", {"start": v(-14701.46, 2851) * mm, "end": v(-15251.46, 2851) * mm});
            skLineSegment(sketch, "E205.MirrorCS", {"start": v(-17701.46, 2851) * mm, "end": v(-18251.46, 2851) * mm});
            skLineSegment(sketch, "E206.MirrorCS", {"start": v(-17701.46, 3201) * mm, "end": v(-17701.46, 2851) * mm});
            skLineSegment(sketch, "E207.MirrorCS", {"start": v(-17701.46, 3201) * mm, "end": v(-18251.46, 3201) * mm});
            skArc(sketch, "E208.MirrorCS", {"start": v(-18251.46, 3201) * mm, "mid": v(-18375.2, 3252.26) * mm, "end": v(-18426.46, 3376) * mm});
            skArc(sketch, "E209.MirrorCS", {"start": v(-18251.46, 2851) * mm, "mid": v(-18622.7, 3004.77) * mm, "end": v(-18776.46, 3376) * mm});
            skLineSegment(sketch, "E210.MirrorCS", {"start": v(-18426.46, 3376) * mm, "end": v(-18426.46, 4326) * mm});
            skLineSegment(sketch, "E211.MirrorCS", {"start": v(-18776.46, 3376) * mm, "end": v(-18776.46, 4326) * mm});
            skLineSegment(sketch, "E212.MirrorCS", {"start": v(-18776.46, 4326) * mm, "end": v(-18851.46, 4551) * mm});
            skLineSegment(sketch, "E213.MirrorCS", {"start": v(-18426.46, 4326) * mm, "end": v(-18351.46, 4551) * mm});
            skLineSegment(sketch, "E214.MirrorCS", {"start": v(-18351.46, 4551) * mm, "end": v(-18851.46, 4551) * mm});
            skSolve(sketch);
        }
        {
            var Q0;
            {var subQ0=sQuery(id+"F1.wireOp",EDGE,"E151.trimOffspring");var subQ1=sQuery(id+"F1.wireOp",EDGE,"E83.0");var subQ2=sQuery(id+"F1.wireOp",EDGE,"E85");var subQ4=sQuery(id+"F1.wireOp",EDGE,"E154");var subQ5=sQuery(id+"F1.wireOp",EDGE,"E82.0");var subQ7=sQuery(id+"F1.wireOp",EDGE,"E155.trimOffspring");var subQ8=sQuery(id+"F1.wireOp",EDGE,"E81.0");var subQ10=sQuery(id+"F1.wireOp",EDGE,"E150.trimOffspring");var subQ11=sQuery(id+"F1.wireOp",EDGE,"E80.0");var subQ13=sQuery(id+"F1.wireOp",EDGE,"E153");var subQ14=sQuery(id+"F1.wireOp",EDGE,"E79.0");var subQ16=sQuery(id+"F1.wireOp",EDGE,"E152");var subQ17=sQuery(id+"F1.wireOp",EDGE,"E78.0");var subQ19=sQuery(id+"F1.wireOp",EDGE,"E149.trimOffspring");var subQ20=sQuery(id+"F1.wireOp",EDGE,"E77.0");var subQ22=sQuery(id+"F1.wireOp",EDGE,"E148.trimOffspring");var subQ23=sQuery(id+"F1.wireOp",EDGE,"E76.0");var subQ25=sQuery(id+"F1.wireOp",EDGE,"E147.trimOffspring");var subQ26=sQuery(id+"F1.wireOp",EDGE,"E75.0");var subQ28=sQuery(id+"F1.wireOp",EDGE,"E145.trimOffspring");var subQ29=sQuery(id+"F1.wireOp",EDGE,"E74.0");var subQ31=sQuery(id+"F1.wireOp",EDGE,"E146.trimOffspring");var subQ32=sQuery(id+"F1.wireOp",EDGE,"E73.0");var subQ34=sQuery(id+"F1.wireOp",EDGE,"E144.trimOffspring");var subQ35=sQuery(id+"F1.wireOp",EDGE,"E72.0");var subQ37=sQuery(id+"F1.wireOp",EDGE,"E163");var subQ38=sQuery(id+"F1.wireOp",EDGE,"E71.0");var subQ40=sQuery(id+"F1.wireOp",EDGE,"E143.trimOffspring");var subQ41=sQuery(id+"F1.wireOp",EDGE,"E70.0");var subQ43=sQuery(id+"F1.wireOp",EDGE,"E142.trimOffspring");var subQ44=sQuery(id+"F1.wireOp",EDGE,"E69.0");var subQ46=sQuery(id+"F1.wireOp",EDGE,"E139.trimOffspring");var subQ47=sQuery(id+"F1.wireOp",EDGE,"E68.0");var subQ49=sQuery(id+"F1.wireOp",EDGE,"E140.trimOffspring");var subQ50=sQuery(id+"F1.wireOp",EDGE,"E67.0");var subQ52=sQuery(id+"F1.wireOp",EDGE,"E138.trimOffspring");var subQ53=sQuery(id+"F1.wireOp",EDGE,"E66.0");var subQ55=sQuery(id+"F1.wireOp",EDGE,"E141");var subQ56=sQuery(id+"F1.wireOp",EDGE,"E65.0");var subQ58=sQuery(id+"F1.wireOp",EDGE,"E134.trimOffspring");var subQ59=sQuery(id+"F1.wireOp",EDGE,"E64.0");var subQ61=sQuery(id+"F1.wireOp",EDGE,"E137");var subQ62=sQuery(id+"F1.wireOp",EDGE,"E63.0");var subQ64=sQuery(id+"F1.wireOp",EDGE,"E135.trimOffspring");var subQ65=sQuery(id+"F1.wireOp",EDGE,"E62.0");var subQ71=sQuery(id+"F1.wireOp",EDGE,"E19.0");var subQ73=sQuery(id+"F1.wireOp",EDGE,"E58.0");var subQ75=sQuery(id+"F1.wireOp",EDGE,"E159");var subQ76=sQuery(id+"F1.wireOp",EDGE,"E9.0");var subQ78=sQuery(id+"F1.wireOp",EDGE,"E136.trimOffspring");var subQ79=sQuery(id+"F1.wireOp",EDGE,"E61.0");var subQ81=sQuery(id+"F1.wireOp",EDGE,"E162");var subQ82=sQuery(id+"F1.wireOp",EDGE,"E17.0");var subQ84=sQuery(id+"F1.wireOp",EDGE,"E56.0");var subQ86=sQuery(id+"F1.wireOp",EDGE,"E158.trimOffspring");var subQ87=sQuery(id+"F1.wireOp",EDGE,"E8.0");var subQ89=sQuery(id+"F1.wireOp",EDGE,"E133.trimOffspring");var subQ90=sQuery(id+"F1.wireOp",EDGE,"E60.0");var subQ92=sQuery(id+"F1.wireOp",EDGE,"E160");var subQ93=sQuery(id+"F1.wireOp",EDGE,"E15.0");var subQ95=sQuery(id+"F1.wireOp",EDGE,"E54.0");var subQ97=sQuery(id+"F1.wireOp",EDGE,"E125.trimOffspring");var subQ98=sQuery(id+"F1.wireOp",EDGE,"E7.0");var subQ100=sQuery(id+"F1.wireOp",EDGE,"E161");var subQ101=sQuery(id+"F1.wireOp",EDGE,"E59.0");var subQ103=sQuery(id+"F1.wireOp",EDGE,"E13.0");var subQ105=sQuery(id+"F1.wireOp",EDGE,"E52.0");var subQ107=sQuery(id+"F1.wireOp",EDGE,"E6.0");var subQ109=sQuery(id+"F1.wireOp",EDGE,"E129.trimOffspring");var subQ110=sQuery(id+"F1.wireOp",EDGE,"E156.trimOffspring");var subQ111=sQuery(id+"F1.wireOp",EDGE,"E11.0");var subQ113=sQuery(id+"F1.wireOp",EDGE,"E50.0");var subQ115=sQuery(id+"F1.wireOp",EDGE,"E5.0");var subQ116=sQuery(id+"F1.wireOp",EDGE,"E3");var subQ118=sQuery(id+"F1.wireOp",EDGE,"E132");var subQ119=sQuery(id+"F1.wireOp",EDGE,"E57.0");var subQ121=sQuery(id+"F1.wireOp",EDGE,"E48.0");var subQ123=sQuery(id+"F1.wireOp",EDGE,"E4");var subQ124=sQuery(id+"F1.wireOp",EDGE,"E130.trimOffspring");var subQ125=sQuery(id+"F1.wireOp",EDGE,"E46.0");var subQ127=sQuery(id+"F1.wireOp",EDGE,"E2");var subQ128=sQuery(id+"F1.wireOp",EDGE,"E128.trimOffspring");var subQ129=sQuery(id+"F1.wireOp",EDGE,"E55.0");var subQ131=sQuery(id+"F1.wireOp",EDGE,"E131");var subQ132=sQuery(id+"F1.wireOp",EDGE,"E157.trimOffspring");var subQ133=sQuery(id+"F1.wireOp",EDGE,"E51.0");var subQ135=sQuery(id+"F1.wireOp",EDGE,"E126.trimOffspring");var subQ136=sQuery(id+"F1.wireOp",EDGE,"E49.0");var subQ138=sQuery(id+"F1.wireOp",EDGE,"E24.0");var subQ140=sQuery(id+"F1.wireOp",EDGE,"E23.0");var subQ142=sQuery(id+"F1.wireOp",EDGE,"E22.0");var subQ144=sQuery(id+"F1.wireOp",EDGE,"E44.0");var subQ146=sQuery(id+"F1.wireOp",EDGE,"E20.0");var subQ148=sQuery(id+"F1.wireOp",EDGE,"E42.0");var subQ150=sQuery(id+"F1.wireOp",EDGE,"E40.0");var subQ152=sQuery(id+"F1.wireOp",EDGE,"E18.0");var subQ154=sQuery(id+"F1.wireOp",EDGE,"E38.0");var subQ156=sQuery(id+"F1.wireOp",EDGE,"E36.0");var subQ158=sQuery(id+"F1.wireOp",EDGE,"E16.0");var subQ160=sQuery(id+"F1.wireOp",EDGE,"E34.0");var subQ162=sQuery(id+"F1.wireOp",EDGE,"E14.0");var subQ164=sQuery(id+"F1.wireOp",EDGE,"E30.0");var subQ166=sQuery(id+"F1.wireOp",EDGE,"E127.trimOffspring");var subQ167=sQuery(id+"F1.wireOp",EDGE,"E28.0");var subQ169=sQuery(id+"F1.wireOp",EDGE,"E12.0");var subQ171=sQuery(id+"F1.wireOp",EDGE,"E26.0");var subQ173=sQuery(id+"F1.wireOp",EDGE,"E32.0");var subQ175=sQuery(id+"F1.wireOp",EDGE,"E53.0");var subQ177=sQuery(id+"F1.wireOp",EDGE,"E47.0");var subQ179=sQuery(id+"F1.wireOp",EDGE,"E10.0");var subQ181=sQuery(id+"F1.wireOp",EDGE,"E25.0");var subQ183=sQuery(id+"F1.wireOp",EDGE,"E27.0");var subQ185=sQuery(id+"F1.wireOp",EDGE,"E29.0");var subQ187=sQuery(id+"F1.wireOp",EDGE,"E31.0");var subQ189=sQuery(id+"F1.wireOp",EDGE,"E33.0");var subQ191=sQuery(id+"F1.wireOp",EDGE,"E35.0");var subQ193=sQuery(id+"F1.wireOp",EDGE,"E37.0");var subQ195=sQuery(id+"F1.wireOp",EDGE,"E39.0");var subQ197=sQuery(id+"F1.wireOp",EDGE,"E41.0");var subQ199=sQuery(id+"F1.wireOp",EDGE,"E43.0");var subQ201=sQuery(id+"F1.wireOp",EDGE,"E45.0");Q0=makeQuery(id+"F9.boolean.opBoolean","SPLIT",FACE,{"disambiguationData":[TD([makeQuery(id+"F2.opExtrude","SWEPT_FACE",FACE,{"disambiguationData":[OSD([subQ116])]})])],"derivedFrom":makeQuery(id+"F2.opExtrude","CAP_FACE",FACE,{"disambiguationData":[OSD([sQuery(id+"F1.wireOp",EDGE,"E1"),subQ127,subQ116,subQ123,subQ115,subQ107,subQ98,subQ87,subQ76,subQ179,subQ111,subQ169,subQ103,subQ162,subQ93,subQ158,subQ82,subQ152,subQ71,subQ146,subQ142,subQ140,subQ138,subQ181,subQ171,subQ183,subQ167,subQ185,subQ164,subQ187,subQ173,subQ189,subQ160,subQ191,subQ156,subQ193,subQ154,subQ195,subQ150,subQ197,subQ148,subQ199,subQ144,subQ201,subQ125,subQ177,subQ121,subQ136,subQ113,subQ133,subQ105,subQ175,subQ95,subQ129,subQ84,subQ119,subQ73,subQ101,subQ90,subQ79,subQ65,subQ62,subQ59,subQ56,subQ53,subQ50,subQ47,subQ44,subQ41,subQ38,subQ35,subQ32,subQ29,subQ26,subQ23,subQ20,subQ17,subQ14,subQ11,subQ8,subQ5,subQ1,sQuery(id+"F1.wireOp",EDGE,"E84"),subQ2,sQuery(id+"F1.wireOp",EDGE,"E86.trimOffspring"),sQuery(id+"F1.wireOp",EDGE,"E87.trimOffspring"),sQuery(id+"F1.wireOp",EDGE,"E88.trimOffspring"),sQuery(id+"F1.wireOp",EDGE,"E89.trimOffspring"),sQuery(id+"F1.wireOp",EDGE,"E90.trimOffspring"),sQuery(id+"F1.wireOp",EDGE,"E91.trimOffspring"),sQuery(id+"F1.wireOp",EDGE,"E92.trimOffspring"),sQuery(id+"F1.wireOp",EDGE,"E93.trimOffspring"),sQuery(id+"F1.wireOp",EDGE,"E94.trimOffspring"),sQuery(id+"F1.wireOp",EDGE,"E95.trimOffspring"),sQuery(id+"F1.wireOp",EDGE,"E96.trimOffspring"),sQuery(id+"F1.wireOp",EDGE,"E97.trimOffspring"),sQuery(id+"F1.wireOp",EDGE,"E98.trimOffspring"),sQuery(id+"F1.wireOp",EDGE,"E99.trimOffspring"),sQuery(id+"F1.wireOp",EDGE,"E100.trimOffspring"),sQuery(id+"F1.wireOp",EDGE,"E101.trimOffspring"),sQuery(id+"F1.wireOp",EDGE,"E102.trimOffspring"),sQuery(id+"F1.wireOp",EDGE,"E103.trimOffspring"),sQuery(id+"F1.wireOp",EDGE,"E104.trimOffspring"),sQuery(id+"F1.wireOp",EDGE,"E105.trimOffspring"),sQuery(id+"F1.wireOp",EDGE,"E106.trimOffspring"),sQuery(id+"F1.wireOp",EDGE,"E107.trimOffspring"),sQuery(id+"F1.wireOp",EDGE,"E108.trimOffspring"),sQuery(id+"F1.wireOp",EDGE,"E109.trimOffspring"),sQuery(id+"F1.wireOp",EDGE,"E110.trimOffspring"),sQuery(id+"F1.wireOp",EDGE,"E111.trimOffspring"),sQuery(id+"F1.wireOp",EDGE,"E112.trimOffspring"),sQuery(id+"F1.wireOp",EDGE,"E113.trimOffspring"),sQuery(id+"F1.wireOp",EDGE,"E114.trimOffspring"),sQuery(id+"F1.wireOp",EDGE,"E115.trimOffspring"),sQuery(id+"F1.wireOp",EDGE,"E116.trimOffspring"),sQuery(id+"F1.wireOp",EDGE,"E117.trimOffspring"),sQuery(id+"F1.wireOp",EDGE,"E118.trimOffspring"),sQuery(id+"F1.wireOp",EDGE,"E119.trimOffspring"),sQuery(id+"F1.wireOp",EDGE,"E120.trimOffspring"),sQuery(id+"F1.wireOp",EDGE,"E121.trimOffspring"),sQuery(id+"F1.wireOp",EDGE,"E122.trimOffspring"),sQuery(id+"F1.wireOp",EDGE,"E123.trimOffspring"),sQuery(id+"F1.wireOp",EDGE,"E124.trimOffspring"),subQ97,subQ135,subQ166,subQ128,subQ109,subQ124,subQ131,subQ118,subQ89,subQ58,subQ64,subQ78,subQ61,subQ52,subQ46,subQ49,subQ55,subQ43,subQ40,subQ34,subQ28,subQ31,subQ25,subQ22,subQ19,subQ10,subQ0,subQ16,subQ13,subQ4,subQ7,subQ110,subQ132,subQ86,subQ75,subQ92,subQ100,subQ81,subQ37])],"isStart":false})});}
            var sketch = newSketch(context, id + "F13", { "sketchPlane" : qUnion([Q0])});
            skLineSegment(sketch, "E215", {"start": v(-20201.46, 3843) * mm, "end": v(-16976.46, 3843) * mm});
            skLineSegment(sketch, "E216", {"start": v(-8476.46, 3843) * mm, "end": v(-8476.46, 4193) * mm});
            skLineSegment(sketch, "E217", {"start": v(-8476.46, 4193) * mm, "end": v(-15926.46, 4193) * mm});
            skLineSegment(sketch, "E218", {"start": v(-20201.46, 4193) * mm, "end": v(-20201.46, 3843) * mm});
            skLineSegment(sketch, "E219", {"start": v(-16976.46, 3843) * mm, "end": v(-16976.46, 3643) * mm});
            skLineSegment(sketch, "E220", {"start": v(-15926.46, 3843) * mm, "end": v(-15926.46, 3643) * mm});
            skLineSegment(sketch, "E221.trimOffspring", {"start": v(-15926.46, 3843) * mm, "end": v(-8476.46, 3843) * mm});
            skArc(sketch, "E222", {"start": v(-15926.46, 4193) * mm, "mid": v(-16252.3, 4086.1) * mm, "end": v(-16451.46, 3806.94) * mm});
            skArc(sketch, "E223", {"start": v(-16451.46, 3806.94) * mm, "mid": v(-16650.63, 4086.1) * mm, "end": v(-16976.46, 4193) * mm});
            skLineSegment(sketch, "E224.trimOffspring", {"start": v(-16976.46, 4193) * mm, "end": v(-20201.46, 4193) * mm});
            skPoint(sketch, "E225.end.orphan", {"position": v(-16451.46, 3643) * mm});
            skLineSegment(sketch, "E226", {"start": v(-16976.46, 3643) * mm, "end": v(-15926.46, 3643) * mm});
            skSolve(sketch);
        }
        {
            var Q0;
            Q0=makeQuery(id+"F13.imprint","IMPRINT",FACE,{"disambiguationData":[TD([[makeQuery(id+"F13.imprint","IMPRINT",EDGE,{"derivedFrom":sQuery(id+"F13.wireOp",EDGE,"E215")}),1.0]])]});
            extrude(context, id + "F14", {"entities" : qUnion([Q0]), "operationType" : NewBodyOperationType.ADD, "depth" : 500 * mm, "offsetDistance" : 25 * mm});
        }
        {
            var Q0;
            Q0 = qSketchRegion(id + "F12", true);
            extrude(context, id + "F15", {"entities" : qUnion([Q0]), "oppositeDirection" : true, "depth" : 500 * mm, "offsetDistance" : 25 * mm});
        }
        {
            var Q0;
            Q0=makeQuery(id+"F15.opExtrude","CAP_FACE",FACE,{"disambiguationData":[OSD([sQuery(id+"F12.wireOp",EDGE,"E193"),sQuery(id+"F12.wireOp",EDGE,"E194"),sQuery(id+"F12.wireOp",EDGE,"E195"),sQuery(id+"F12.wireOp",EDGE,"E196"),sQuery(id+"F12.wireOp",EDGE,"E197.filletArc"),sQuery(id+"F12.wireOp",EDGE,"E198.filletArc"),sQuery(id+"F12.wireOp",EDGE,"E199"),sQuery(id+"F12.wireOp",EDGE,"E200"),sQuery(id+"F12.wireOp",EDGE,"E201"),sQuery(id+"F12.wireOp",EDGE,"E202")])],"isStart":true});
            var sketch = newSketch(context, id + "F16", { "sketchPlane" : qUnion([Q0])});
            skLineSegment(sketch, "E227", {"start": v(-14051.46, 4551) * mm, "end": v(-14051.46, 4901) * mm});
            skLineSegment(sketch, "E228", {"start": v(-14051.46, 4901) * mm, "end": v(-13551.46, 4901) * mm});
            skLineSegment(sketch, "E229", {"start": v(-13551.46, 4901) * mm, "end": v(-13551.46, 4551) * mm});
            skLineSegment(sketch, "E230", {"start": v(-13551.46, 4551) * mm, "end": v(-14051.46, 4551) * mm});
            skLineSegment(sketch, "E231", {"start": v(-14051.46, 4551) * mm, "end": v(-16201.46, 4551) * mm});
            skLineSegment(sketch, "E232", {"start": v(-16201.46, 4551) * mm, "end": v(-16201.46, 2846.64) * mm});
            skLineSegment(sketch, "E233.MirrorCS", {"start": v(-18851.46, 4551) * mm, "end": v(-18351.46, 4551) * mm});
            skLineSegment(sketch, "E234.MirrorCS", {"start": v(-18351.46, 4551) * mm, "end": v(-18351.46, 4901) * mm});
            skLineSegment(sketch, "E235.MirrorCS", {"start": v(-18351.46, 4901) * mm, "end": v(-18851.46, 4901) * mm});
            skLineSegment(sketch, "E236.MirrorCS", {"start": v(-18851.46, 4901) * mm, "end": v(-18851.46, 4551) * mm});
            skSolve(sketch);
        }
        {
            var Q0;
            Q0=makeQuery(id+"F16.imprint","IMPRINT",FACE,{"disambiguationData":[TD([[makeQuery(id+"F16.imprint","IMPRINT",EDGE,{"derivedFrom":sQuery(id+"F16.wireOp",EDGE,"E233.MirrorCS")}),1.0]])]});
            var Q1;
            Q1=makeQuery(id+"F16.imprint","IMPRINT",FACE,{"disambiguationData":[TD([[makeQuery(id+"F16.imprint","IMPRINT",EDGE,{"derivedFrom":sQuery(id+"F16.wireOp",EDGE,"E227")}),-1.0]])]});
            extrude(context, id + "F17", {"entities" : qUnion([Q0, Q1]), "oppositeDirection" : true, "depth" : 544 * mm, "offsetDistance" : 25 * mm});
        }
    });
